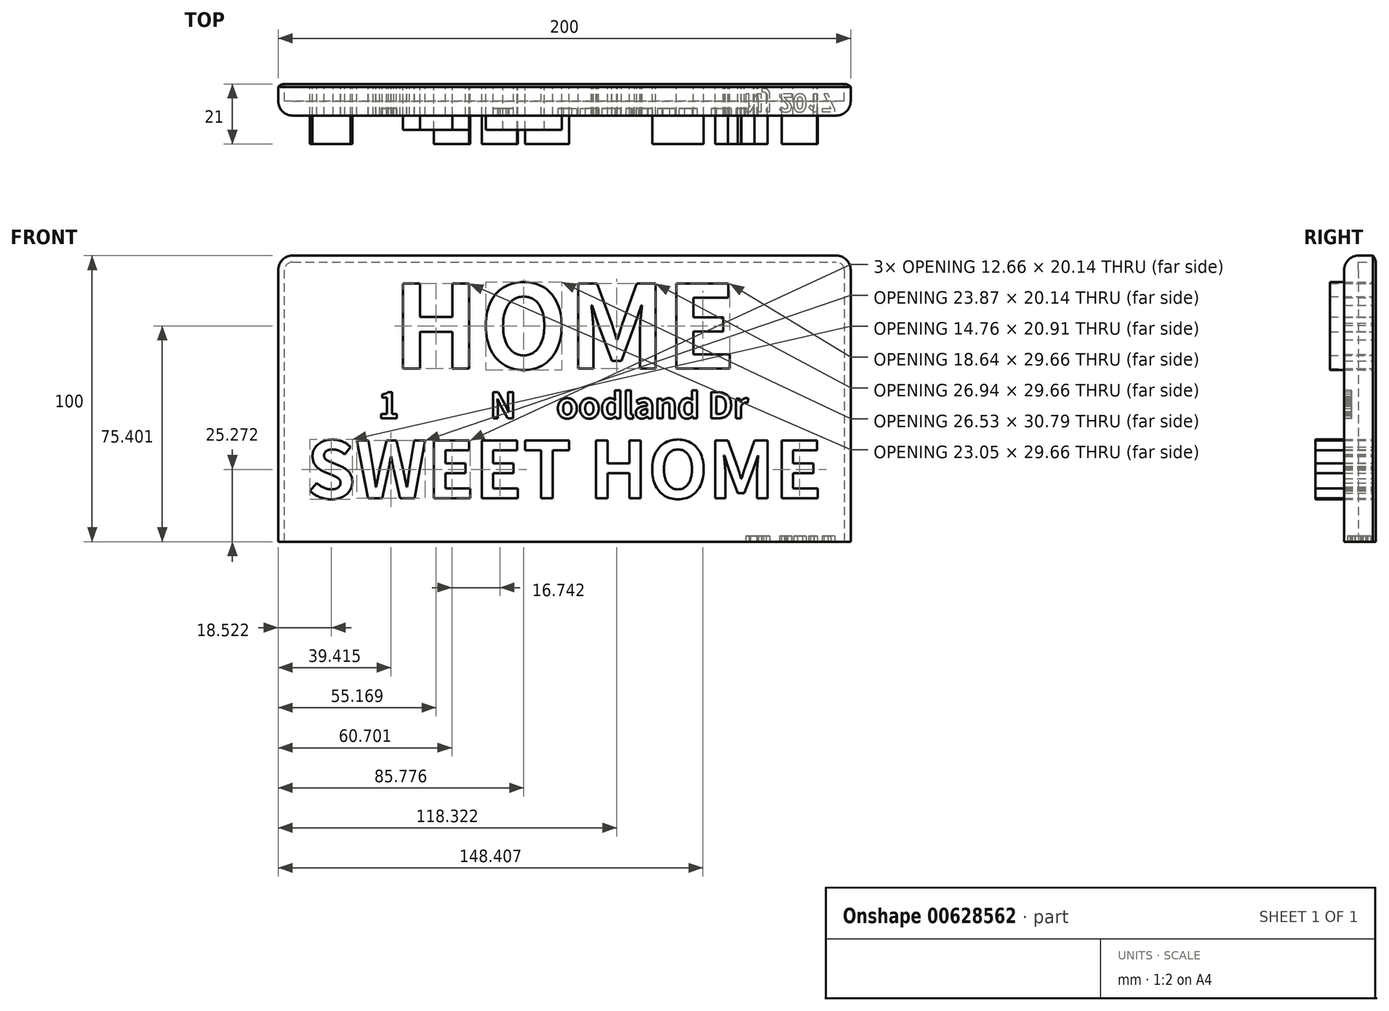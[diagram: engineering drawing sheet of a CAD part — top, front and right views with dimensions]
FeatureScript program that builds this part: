
annotation { "Feature Type Name" : "Feature", "Feature Type Description" : "" }
export const myFeature = defineFeature(function(context is Context, id is Id, definition is map)
    precondition{}
    {
        {
            var Q0;
            Q0=qCreatedBy(makeId("Front.planeOp"),FACE);
            var sketch = newSketch(context, id + "F0", { "sketchPlane" : qUnion([Q0])});
            skLineSegment(sketch, "E0.bottom", {"start": v(100, -50) * mm, "end": v(-100, -50) * mm});
            skLineSegment(sketch, "E0.top", {"start": v(100, 50) * mm, "end": v(-100, 50) * mm});
            skLineSegment(sketch, "E0.left", {"start": v(100, -50) * mm, "end": v(100, 50) * mm});
            skLineSegment(sketch, "E0.right", {"start": v(-100, -50) * mm, "end": v(-100, 50) * mm});
            skPoint(sketch, "E0.middle", {"position": v(0, 0) * mm});
            skLineSegment(sketch, "E1", {"start": v(-100, 0) * mm, "end": v(100, 0) * mm, "construction": true});
            skLineSegment(sketch, "E2", {"start": v(0, 50) * mm, "end": v(0, -50) * mm, "construction": true});
            skText(sketch, "E3", { "text": "HOME", "fontName": "NotoSansCJKsc-Bold.otf"});
            skText(sketch, "E4", { "text": "SWEET HOME", "fontName": "NotoSansCJKsc-Bold.otf"});
            skLineSegment(sketch, "E5", {"start": v(100, 50) * mm, "end": v(100, 25) * mm, "construction": true});
            skLineSegment(sketch, "E6", {"start": v(100, 25) * mm, "end": v(-100, 25) * mm, "construction": true});
            skLineSegment(sketch, "E7", {"start": v(100, 0) * mm, "end": v(100, -25) * mm, "construction": true});
            skLineSegment(sketch, "E8", {"start": v(100, -25) * mm, "end": v(-100, -25) * mm, "construction": true});
            skPoint(sketch, "E8.endSnap0", {"position": v(-90, -25) * mm});
            const initialGuessF0  = {"E3": [-0.06, 0.01057, 1, 0, 0.02886], "E4": [-0.09, -0.0348, 1, 0, 0.0196]};
            skSetInitialGuess(sketch, initialGuessF0);
            skSolve(sketch);
        }
        {
            var Q0;
            Q0=makeQuery(id+"F0.imprint","IMPRINT",FACE,{"disambiguationData":[TD([[makeQuery(id+"F0.imprint","IMPRINT",EDGE,{"derivedFrom":sQuery(id+"F0.wireOp",EDGE,"E4.sketch_text.stroke-0")}),1.0]])]});
            var Q1;
            Q1=makeQuery(id+"F0.imprint","IMPRINT",FACE,{"disambiguationData":[TD([[makeQuery(id+"F0.imprint","IMPRINT",EDGE,{"derivedFrom":sQuery(id+"F0.wireOp",EDGE,"E4.sketch_text.stroke-10")}),1.0]])]});
            var Q2;
            Q2=makeQuery(id+"F0.imprint","IMPRINT",FACE,{"disambiguationData":[TD([[makeQuery(id+"F0.imprint","IMPRINT",EDGE,{"derivedFrom":sQuery(id+"F0.wireOp",EDGE,"E4.sketch_text.stroke-22")}),1.0]])]});
            var Q3;
            Q3=makeQuery(id+"F0.imprint","IMPRINT",FACE,{"disambiguationData":[TD([[makeQuery(id+"F0.imprint","IMPRINT",EDGE,{"derivedFrom":sQuery(id+"F0.wireOp",EDGE,"E4.sketch_text.stroke-32")}),1.0]])]});
            var Q4;
            Q4=makeQuery(id+"F0.imprint","IMPRINT",FACE,{"disambiguationData":[TD([[makeQuery(id+"F0.imprint","IMPRINT",EDGE,{"derivedFrom":sQuery(id+"F0.wireOp",EDGE,"E4.sketch_text.stroke-38")}),1.0]])]});
            var Q5;
            Q5=makeQuery(id+"F0.imprint","IMPRINT",FACE,{"disambiguationData":[TD([[makeQuery(id+"F0.imprint","IMPRINT",EDGE,{"derivedFrom":sQuery(id+"F0.wireOp",EDGE,"E4.sketch_text.stroke-46")}),1.0]])]});
            var Q6;
            Q6=makeQuery(id+"F0.imprint","IMPRINT",FACE,{"disambiguationData":[TD([[makeQuery(id+"F0.imprint","IMPRINT",EDGE,{"derivedFrom":sQuery(id+"F0.wireOp",EDGE,"E4.sketch_text.stroke-62")}),1.0]])]});
            var Q7;
            Q7=makeQuery(id+"F0.imprint","IMPRINT",FACE,{"disambiguationData":[TD([[makeQuery(id+"F0.imprint","IMPRINT",EDGE,{"derivedFrom":sQuery(id+"F0.wireOp",EDGE,"E4.sketch_text.stroke-74")}),1.0]])]});
            var Q8;
            Q8=makeQuery(id+"F0.imprint","IMPRINT",FACE,{"disambiguationData":[TD([[makeQuery(id+"F0.imprint","IMPRINT",EDGE,{"derivedFrom":sQuery(id+"F0.wireOp",EDGE,"E4.sketch_text.stroke-50")}),1.0]])]});
            var Q9;
            Q9=makeQuery(id+"F0.imprint","IMPRINT",FACE,{"disambiguationData":[TD([[makeQuery(id+"F0.imprint","IMPRINT",EDGE,{"derivedFrom":sQuery(id+"F0.wireOp",EDGE,"E4.sketch_text.stroke-82")}),1.0]])]});
            var Q10;
            Q10=makeQuery(id+"F0.imprint","IMPRINT",FACE,{"disambiguationData":[TD([[makeQuery(id+"F0.imprint","IMPRINT",EDGE,{"derivedFrom":sQuery(id+"F0.wireOp",EDGE,"E4.sketch_text.stroke-90")}),1.0]])]});
            var Q11;
            Q11=makeQuery(id+"F0.imprint","IMPRINT",FACE,{"disambiguationData":[TD([[makeQuery(id+"F0.imprint","IMPRINT",EDGE,{"derivedFrom":sQuery(id+"F0.wireOp",EDGE,"E4.sketch_text.stroke-112")}),1.0]])]});
            extrude(context, id + "F1", {"entities" : qUnion([Q0, Q1, Q2, Q3, Q4, Q5, Q6, Q7, Q8, Q9, Q10, Q11]), "depth" : 20 * mm, "offsetDistance" : 25 * mm});
        }
        {
            var Q0;
            Q0=makeQuery(id+"F0.imprint","IMPRINT",FACE,{"disambiguationData":[TD([[makeQuery(id+"F0.imprint","IMPRINT",EDGE,{"derivedFrom":sQuery(id+"F0.wireOp",EDGE,"E3.sketch_text.stroke-0")}),1.0]])]});
            var Q1;
            Q1=makeQuery(id+"F0.imprint","IMPRINT",FACE,{"disambiguationData":[TD([[makeQuery(id+"F0.imprint","IMPRINT",EDGE,{"derivedFrom":sQuery(id+"F0.wireOp",EDGE,"E3.sketch_text.stroke-4")}),1.0]])]});
            var Q2;
            Q2=makeQuery(id+"F0.imprint","IMPRINT",FACE,{"disambiguationData":[TD([[makeQuery(id+"F0.imprint","IMPRINT",EDGE,{"derivedFrom":sQuery(id+"F0.wireOp",EDGE,"E3.sketch_text.stroke-12")}),1.0]])]});
            var Q3;
            Q3=makeQuery(id+"F0.imprint","IMPRINT",FACE,{"disambiguationData":[TD([[makeQuery(id+"F0.imprint","IMPRINT",EDGE,{"derivedFrom":sQuery(id+"F0.wireOp",EDGE,"E3.sketch_text.stroke-34")}),1.0]])]});
            var Q4;
            Q4=makeQuery(id+"F0.imprint","IMPRINT",FACE,{"disambiguationData":[TD([[makeQuery(id+"F0.imprint","IMPRINT",EDGE,{"derivedFrom":sQuery(id+"F0.wireOp",EDGE,"E3.sketch_text.stroke-48")}),1.0]])]});
            var Q5;
            Q5=makeQuery(id+"F0.imprint","IMPRINT",FACE,{"disambiguationData":[TD([[makeQuery(id+"F0.imprint","IMPRINT",EDGE,{"derivedFrom":sQuery(id+"F0.wireOp",EDGE,"E3.sketch_text.stroke-64")}),1.0]])]});
            var Q6;
            Q6=makeQuery(id+"F0.imprint","IMPRINT",FACE,{"disambiguationData":[TD([[makeQuery(id+"F0.imprint","IMPRINT",EDGE,{"derivedFrom":sQuery(id+"F0.wireOp",EDGE,"E3.sketch_text.stroke-72")}),1.0]])]});
            var Q7;
            Q7=makeQuery(id+"F0.imprint","IMPRINT",FACE,{"disambiguationData":[TD([[makeQuery(id+"F0.imprint","IMPRINT",EDGE,{"derivedFrom":sQuery(id+"F0.wireOp",EDGE,"E3.sketch_text.stroke-86")}),1.0]])]});
            var Q8;
            Q8=makeQuery(id+"F0.imprint","IMPRINT",FACE,{"disambiguationData":[TD([[makeQuery(id+"F0.imprint","IMPRINT",EDGE,{"derivedFrom":sQuery(id+"F0.wireOp",EDGE,"E3.sketch_text.stroke-94")}),1.0]])]});
            extrude(context, id + "F2", {"entities" : qUnion([Q0, Q1, Q2, Q3, Q4, Q5, Q6, Q7, Q8]), "depth" : 15 * mm, "offsetDistance" : 25 * mm});
        }
        {
            var Q0;
            Q0=makeQuery(id+"F0.imprint","IMPRINT",FACE,{"disambiguationData":[TD([[makeQuery(id+"F0.imprint","IMPRINT",EDGE,{"derivedFrom":sQuery(id+"F0.wireOp",EDGE,"E3.sketch_text.stroke-8")}),-1.0]])]});
            var Q1;
            Q1=makeQuery(id+"F0.imprint","IMPRINT",FACE,{"disambiguationData":[TD([[makeQuery(id+"F0.imprint","IMPRINT",EDGE,{"derivedFrom":sQuery(id+"F0.wireOp",EDGE,"E3.sketch_text.stroke-34")}),-1.0]])]});
            var Q2;
            Q2=makeQuery(id+"F0.imprint","IMPRINT",FACE,{"disambiguationData":[TD([[makeQuery(id+"F0.imprint","IMPRINT",EDGE,{"derivedFrom":sQuery(id+"F0.wireOp",EDGE,"E3.sketch_text.stroke-72")}),-1.0]])]});
            var Q3;
            Q3=makeQuery(id+"F0.imprint","IMPRINT",FACE,{"disambiguationData":[TD([[makeQuery(id+"F0.imprint","IMPRINT",EDGE,{"derivedFrom":sQuery(id+"F0.wireOp",EDGE,"E4.sketch_text.stroke-42")}),-1.0]])]});
            var Q4;
            Q4=makeQuery(id+"F0.imprint","IMPRINT",FACE,{"disambiguationData":[TD([[makeQuery(id+"F0.imprint","IMPRINT",EDGE,{"derivedFrom":sQuery(id+"F0.wireOp",EDGE,"E0.bottom")}),-1.0]])]});
            extrude(context, id + "F3", {"entities" : qUnion([Q0, Q1, Q2, Q3, Q4]), "depth" : 10 * mm, "offsetDistance" : 25 * mm});
        }
        {
            var Q0;
            Q0=makeQuery(id+"F3.opExtrude","CAP_FACE",FACE,{"disambiguationData":[OSD([sQuery(id+"F0.wireOp",EDGE,"E0.bottom"),sQuery(id+"F0.wireOp",EDGE,"E0.top"),sQuery(id+"F0.wireOp",EDGE,"E0.left"),sQuery(id+"F0.wireOp",EDGE,"E0.right"),sQuery(id+"F0.wireOp",EDGE,"E3.sketch_text.stroke-0"),sQuery(id+"F0.wireOp",EDGE,"E3.sketch_text.stroke-1"),sQuery(id+"F0.wireOp",EDGE,"E3.sketch_text.stroke-2"),sQuery(id+"F0.wireOp",EDGE,"E3.sketch_text.stroke-3"),sQuery(id+"F0.wireOp",EDGE,"E3.sketch_text.stroke-4"),sQuery(id+"F0.wireOp",EDGE,"E3.sketch_text.stroke-5"),sQuery(id+"F0.wireOp",EDGE,"E3.sketch_text.stroke-6"),sQuery(id+"F0.wireOp",EDGE,"E3.sketch_text.stroke-7"),sQuery(id+"F0.wireOp",EDGE,"E3.sketch_text.stroke-12"),sQuery(id+"F0.wireOp",EDGE,"E3.sketch_text.stroke-13"),sQuery(id+"F0.wireOp",EDGE,"E3.sketch_text.stroke-14"),sQuery(id+"F0.wireOp",EDGE,"E3.sketch_text.stroke-15"),sQuery(id+"F0.wireOp",EDGE,"E3.sketch_text.stroke-16"),sQuery(id+"F0.wireOp",EDGE,"E3.sketch_text.stroke-17"),sQuery(id+"F0.wireOp",EDGE,"E3.sketch_text.stroke-18"),sQuery(id+"F0.wireOp",EDGE,"E3.sketch_text.stroke-19"),sQuery(id+"F0.wireOp",EDGE,"E3.sketch_text.stroke-20"),sQuery(id+"F0.wireOp",EDGE,"E3.sketch_text.stroke-21"),sQuery(id+"F0.wireOp",EDGE,"E3.sketch_text.stroke-22"),sQuery(id+"F0.wireOp",EDGE,"E3.sketch_text.stroke-23"),sQuery(id+"F0.wireOp",EDGE,"E3.sketch_text.stroke-24"),sQuery(id+"F0.wireOp",EDGE,"E3.sketch_text.stroke-25"),sQuery(id+"F0.wireOp",EDGE,"E3.sketch_text.stroke-26"),sQuery(id+"F0.wireOp",EDGE,"E3.sketch_text.stroke-27"),sQuery(id+"F0.wireOp",EDGE,"E3.sketch_text.stroke-28"),sQuery(id+"F0.wireOp",EDGE,"E3.sketch_text.stroke-29"),sQuery(id+"F0.wireOp",EDGE,"E3.sketch_text.stroke-30"),sQuery(id+"F0.wireOp",EDGE,"E3.sketch_text.stroke-31"),sQuery(id+"F0.wireOp",EDGE,"E3.sketch_text.stroke-32"),sQuery(id+"F0.wireOp",EDGE,"E3.sketch_text.stroke-33"),sQuery(id+"F0.wireOp",EDGE,"E3.sketch_text.stroke-40"),sQuery(id+"F0.wireOp",EDGE,"E3.sketch_text.stroke-41"),sQuery(id+"F0.wireOp",EDGE,"E3.sketch_text.stroke-42"),sQuery(id+"F0.wireOp",EDGE,"E3.sketch_text.stroke-43"),sQuery(id+"F0.wireOp",EDGE,"E3.sketch_text.stroke-44"),sQuery(id+"F0.wireOp",EDGE,"E3.sketch_text.stroke-45"),sQuery(id+"F0.wireOp",EDGE,"E3.sketch_text.stroke-46"),sQuery(id+"F0.wireOp",EDGE,"E3.sketch_text.stroke-47"),sQuery(id+"F0.wireOp",EDGE,"E3.sketch_text.stroke-48"),sQuery(id+"F0.wireOp",EDGE,"E3.sketch_text.stroke-49"),sQuery(id+"F0.wireOp",EDGE,"E3.sketch_text.stroke-50"),sQuery(id+"F0.wireOp",EDGE,"E3.sketch_text.stroke-51"),sQuery(id+"F0.wireOp",EDGE,"E3.sketch_text.stroke-52"),sQuery(id+"F0.wireOp",EDGE,"E3.sketch_text.stroke-53"),sQuery(id+"F0.wireOp",EDGE,"E3.sketch_text.stroke-54"),sQuery(id+"F0.wireOp",EDGE,"E3.sketch_text.stroke-55"),sQuery(id+"F0.wireOp",EDGE,"E3.sketch_text.stroke-56"),sQuery(id+"F0.wireOp",EDGE,"E3.sketch_text.stroke-57"),sQuery(id+"F0.wireOp",EDGE,"E3.sketch_text.stroke-58"),sQuery(id+"F0.wireOp",EDGE,"E3.sketch_text.stroke-59"),sQuery(id+"F0.wireOp",EDGE,"E3.sketch_text.stroke-60"),sQuery(id+"F0.wireOp",EDGE,"E3.sketch_text.stroke-61"),sQuery(id+"F0.wireOp",EDGE,"E3.sketch_text.stroke-62"),sQuery(id+"F0.wireOp",EDGE,"E3.sketch_text.stroke-63"),sQuery(id+"F0.wireOp",EDGE,"E3.sketch_text.stroke-64"),sQuery(id+"F0.wireOp",EDGE,"E3.sketch_text.stroke-65"),sQuery(id+"F0.wireOp",EDGE,"E3.sketch_text.stroke-66"),sQuery(id+"F0.wireOp",EDGE,"E3.sketch_text.stroke-67"),sQuery(id+"F0.wireOp",EDGE,"E3.sketch_text.stroke-68"),sQuery(id+"F0.wireOp",EDGE,"E3.sketch_text.stroke-69"),sQuery(id+"F0.wireOp",EDGE,"E3.sketch_text.stroke-70"),sQuery(id+"F0.wireOp",EDGE,"E3.sketch_text.stroke-71"),sQuery(id+"F0.wireOp",EDGE,"E3.sketch_text.stroke-78"),sQuery(id+"F0.wireOp",EDGE,"E3.sketch_text.stroke-79"),sQuery(id+"F0.wireOp",EDGE,"E3.sketch_text.stroke-80"),sQuery(id+"F0.wireOp",EDGE,"E3.sketch_text.stroke-81"),sQuery(id+"F0.wireOp",EDGE,"E3.sketch_text.stroke-82"),sQuery(id+"F0.wireOp",EDGE,"E3.sketch_text.stroke-83"),sQuery(id+"F0.wireOp",EDGE,"E3.sketch_text.stroke-84"),sQuery(id+"F0.wireOp",EDGE,"E3.sketch_text.stroke-85"),sQuery(id+"F0.wireOp",EDGE,"E3.sketch_text.stroke-86"),sQuery(id+"F0.wireOp",EDGE,"E3.sketch_text.stroke-87"),sQuery(id+"F0.wireOp",EDGE,"E3.sketch_text.stroke-88"),sQuery(id+"F0.wireOp",EDGE,"E3.sketch_text.stroke-89"),sQuery(id+"F0.wireOp",EDGE,"E3.sketch_text.stroke-90"),sQuery(id+"F0.wireOp",EDGE,"E3.sketch_text.stroke-91"),sQuery(id+"F0.wireOp",EDGE,"E3.sketch_text.stroke-92"),sQuery(id+"F0.wireOp",EDGE,"E3.sketch_text.stroke-93"),sQuery(id+"F0.wireOp",EDGE,"E3.sketch_text.stroke-94"),sQuery(id+"F0.wireOp",EDGE,"E3.sketch_text.stroke-95"),sQuery(id+"F0.wireOp",EDGE,"E3.sketch_text.stroke-96"),sQuery(id+"F0.wireOp",EDGE,"E3.sketch_text.stroke-97"),sQuery(id+"F0.wireOp",EDGE,"E3.sketch_text.stroke-98"),sQuery(id+"F0.wireOp",EDGE,"E3.sketch_text.stroke-99"),sQuery(id+"F0.wireOp",EDGE,"E3.sketch_text.stroke-100"),sQuery(id+"F0.wireOp",EDGE,"E3.sketch_text.stroke-101"),sQuery(id+"F0.wireOp",EDGE,"E3.sketch_text.stroke-102"),sQuery(id+"F0.wireOp",EDGE,"E3.sketch_text.stroke-103"),sQuery(id+"F0.wireOp",EDGE,"E3.sketch_text.stroke-104"),sQuery(id+"F0.wireOp",EDGE,"E3.sketch_text.stroke-105"),sQuery(id+"F0.wireOp",EDGE,"E4.sketch_text.stroke-0"),sQuery(id+"F0.wireOp",EDGE,"E4.sketch_text.stroke-1"),sQuery(id+"F0.wireOp",EDGE,"E4.sketch_text.stroke-2"),sQuery(id+"F0.wireOp",EDGE,"E4.sketch_text.stroke-3"),sQuery(id+"F0.wireOp",EDGE,"E4.sketch_text.stroke-4"),sQuery(id+"F0.wireOp",EDGE,"E4.sketch_text.stroke-5"),sQuery(id+"F0.wireOp",EDGE,"E4.sketch_text.stroke-6"),sQuery(id+"F0.wireOp",EDGE,"E4.sketch_text.stroke-7"),sQuery(id+"F0.wireOp",EDGE,"E4.sketch_text.stroke-8"),sQuery(id+"F0.wireOp",EDGE,"E4.sketch_text.stroke-9"),sQuery(id+"F0.wireOp",EDGE,"E4.sketch_text.stroke-10"),sQuery(id+"F0.wireOp",EDGE,"E4.sketch_text.stroke-11"),sQuery(id+"F0.wireOp",EDGE,"E4.sketch_text.stroke-12"),sQuery(id+"F0.wireOp",EDGE,"E4.sketch_text.stroke-13"),sQuery(id+"F0.wireOp",EDGE,"E4.sketch_text.stroke-14"),sQuery(id+"F0.wireOp",EDGE,"E4.sketch_text.stroke-15"),sQuery(id+"F0.wireOp",EDGE,"E4.sketch_text.stroke-16"),sQuery(id+"F0.wireOp",EDGE,"E4.sketch_text.stroke-17"),sQuery(id+"F0.wireOp",EDGE,"E4.sketch_text.stroke-18"),sQuery(id+"F0.wireOp",EDGE,"E4.sketch_text.stroke-19"),sQuery(id+"F0.wireOp",EDGE,"E4.sketch_text.stroke-20"),sQuery(id+"F0.wireOp",EDGE,"E4.sketch_text.stroke-21"),sQuery(id+"F0.wireOp",EDGE,"E4.sketch_text.stroke-22"),sQuery(id+"F0.wireOp",EDGE,"E4.sketch_text.stroke-23"),sQuery(id+"F0.wireOp",EDGE,"E4.sketch_text.stroke-24"),sQuery(id+"F0.wireOp",EDGE,"E4.sketch_text.stroke-25"),sQuery(id+"F0.wireOp",EDGE,"E4.sketch_text.stroke-26"),sQuery(id+"F0.wireOp",EDGE,"E4.sketch_text.stroke-27"),sQuery(id+"F0.wireOp",EDGE,"E4.sketch_text.stroke-28"),sQuery(id+"F0.wireOp",EDGE,"E4.sketch_text.stroke-29"),sQuery(id+"F0.wireOp",EDGE,"E4.sketch_text.stroke-30"),sQuery(id+"F0.wireOp",EDGE,"E4.sketch_text.stroke-31"),sQuery(id+"F0.wireOp",EDGE,"E4.sketch_text.stroke-32"),sQuery(id+"F0.wireOp",EDGE,"E4.sketch_text.stroke-33"),sQuery(id+"F0.wireOp",EDGE,"E4.sketch_text.stroke-34"),sQuery(id+"F0.wireOp",EDGE,"E4.sketch_text.stroke-35"),sQuery(id+"F0.wireOp",EDGE,"E4.sketch_text.stroke-36"),sQuery(id+"F0.wireOp",EDGE,"E4.sketch_text.stroke-37"),sQuery(id+"F0.wireOp",EDGE,"E4.sketch_text.stroke-38"),sQuery(id+"F0.wireOp",EDGE,"E4.sketch_text.stroke-39"),sQuery(id+"F0.wireOp",EDGE,"E4.sketch_text.stroke-40"),sQuery(id+"F0.wireOp",EDGE,"E4.sketch_text.stroke-41"),sQuery(id+"F0.wireOp",EDGE,"E4.sketch_text.stroke-46"),sQuery(id+"F0.wireOp",EDGE,"E4.sketch_text.stroke-47"),sQuery(id+"F0.wireOp",EDGE,"E4.sketch_text.stroke-48"),sQuery(id+"F0.wireOp",EDGE,"E4.sketch_text.stroke-49"),sQuery(id+"F0.wireOp",EDGE,"E4.sketch_text.stroke-50"),sQuery(id+"F0.wireOp",EDGE,"E4.sketch_text.stroke-51"),sQuery(id+"F0.wireOp",EDGE,"E4.sketch_text.stroke-52"),sQuery(id+"F0.wireOp",EDGE,"E4.sketch_text.stroke-53"),sQuery(id+"F0.wireOp",EDGE,"E4.sketch_text.stroke-54"),sQuery(id+"F0.wireOp",EDGE,"E4.sketch_text.stroke-55"),sQuery(id+"F0.wireOp",EDGE,"E4.sketch_text.stroke-56"),sQuery(id+"F0.wireOp",EDGE,"E4.sketch_text.stroke-57"),sQuery(id+"F0.wireOp",EDGE,"E4.sketch_text.stroke-58"),sQuery(id+"F0.wireOp",EDGE,"E4.sketch_text.stroke-59"),sQuery(id+"F0.wireOp",EDGE,"E4.sketch_text.stroke-60"),sQuery(id+"F0.wireOp",EDGE,"E4.sketch_text.stroke-61"),sQuery(id+"F0.wireOp",EDGE,"E4.sketch_text.stroke-62"),sQuery(id+"F0.wireOp",EDGE,"E4.sketch_text.stroke-63"),sQuery(id+"F0.wireOp",EDGE,"E4.sketch_text.stroke-64"),sQuery(id+"F0.wireOp",EDGE,"E4.sketch_text.stroke-65"),sQuery(id+"F0.wireOp",EDGE,"E4.sketch_text.stroke-66"),sQuery(id+"F0.wireOp",EDGE,"E4.sketch_text.stroke-67"),sQuery(id+"F0.wireOp",EDGE,"E4.sketch_text.stroke-68"),sQuery(id+"F0.wireOp",EDGE,"E4.sketch_text.stroke-69"),sQuery(id+"F0.wireOp",EDGE,"E4.sketch_text.stroke-70"),sQuery(id+"F0.wireOp",EDGE,"E4.sketch_text.stroke-71"),sQuery(id+"F0.wireOp",EDGE,"E4.sketch_text.stroke-72"),sQuery(id+"F0.wireOp",EDGE,"E4.sketch_text.stroke-73"),sQuery(id+"F0.wireOp",EDGE,"E4.sketch_text.stroke-74"),sQuery(id+"F0.wireOp",EDGE,"E4.sketch_text.stroke-75"),sQuery(id+"F0.wireOp",EDGE,"E4.sketch_text.stroke-76"),sQuery(id+"F0.wireOp",EDGE,"E4.sketch_text.stroke-77"),sQuery(id+"F0.wireOp",EDGE,"E4.sketch_text.stroke-78"),sQuery(id+"F0.wireOp",EDGE,"E4.sketch_text.stroke-79"),sQuery(id+"F0.wireOp",EDGE,"E4.sketch_text.stroke-80"),sQuery(id+"F0.wireOp",EDGE,"E4.sketch_text.stroke-81"),sQuery(id+"F0.wireOp",EDGE,"E4.sketch_text.stroke-82"),sQuery(id+"F0.wireOp",EDGE,"E4.sketch_text.stroke-83"),sQuery(id+"F0.wireOp",EDGE,"E4.sketch_text.stroke-84"),sQuery(id+"F0.wireOp",EDGE,"E4.sketch_text.stroke-85"),sQuery(id+"F0.wireOp",EDGE,"E4.sketch_text.stroke-86"),sQuery(id+"F0.wireOp",EDGE,"E4.sketch_text.stroke-87"),sQuery(id+"F0.wireOp",EDGE,"E4.sketch_text.stroke-88"),sQuery(id+"F0.wireOp",EDGE,"E4.sketch_text.stroke-89")])],"isStart":false});
            var sketch = newSketch(context, id + "F4", { "sketchPlane" : qUnion([Q0])});
            skText(sketch, "E9", { "text": "12524 N Woodland Dr", "fontName": "NotoSansCJKkr-Bold.otf"});
            skLineSegment(sketch, "E10", {"start": v(-100, 50) * mm, "end": v(100, 50) * mm, "construction": true});
            skLineSegment(sketch, "E11", {"start": v(100, 50) * mm, "end": v(100, -50) * mm, "construction": true});
            skLineSegment(sketch, "E12", {"start": v(100, -50) * mm, "end": v(-100, -50) * mm, "construction": true});
            skLineSegment(sketch, "E13", {"start": v(-100, -50) * mm, "end": v(-100, 50) * mm, "construction": true});
            skLineSegment(sketch, "E14", {"start": v(0, 50) * mm, "end": v(0, -50) * mm, "construction": true});
            skLineSegment(sketch, "E15", {"start": v(-100, 0) * mm, "end": v(100, 0) * mm, "construction": true});
            const initialGuessF4  = {"E9": [-0.065, -0.00684, 1, 0, 0.00884]};
            skSetInitialGuess(sketch, initialGuessF4);
            skSolve(sketch);
        }
        {
            var Q0;
            Q0=makeQuery(id+"F4.imprint","IMPRINT",FACE,{"disambiguationData":[TD([[makeQuery(id+"F4.imprint","IMPRINT",EDGE,{"derivedFrom":sQuery(id+"F4.wireOp",EDGE,"E9.sketch_text.stroke-0")}),1.0]])]});
            var Q1;
            Q1=makeQuery(id+"F4.imprint","IMPRINT",FACE,{"disambiguationData":[TD([[makeQuery(id+"F4.imprint","IMPRINT",EDGE,{"derivedFrom":sQuery(id+"F4.wireOp",EDGE,"E9.sketch_text.stroke-14")}),1.0]])]});
            var Q2;
            Q2=makeQuery(id+"F4.imprint","IMPRINT",FACE,{"disambiguationData":[TD([[makeQuery(id+"F4.imprint","IMPRINT",EDGE,{"derivedFrom":sQuery(id+"F4.wireOp",EDGE,"E9.sketch_text.stroke-29")}),1.0]])]});
            var Q3;
            Q3=makeQuery(id+"F4.imprint","IMPRINT",FACE,{"disambiguationData":[TD([[makeQuery(id+"F4.imprint","IMPRINT",EDGE,{"derivedFrom":sQuery(id+"F4.wireOp",EDGE,"E9.sketch_text.stroke-43")}),1.0]])]});
            var Q4;
            Q4=makeQuery(id+"F4.imprint","IMPRINT",FACE,{"disambiguationData":[TD([[makeQuery(id+"F4.imprint","IMPRINT",EDGE,{"derivedFrom":sQuery(id+"F4.wireOp",EDGE,"E9.sketch_text.stroke-59")}),1.0]])]});
            var Q5;
            Q5=makeQuery(id+"F4.imprint","IMPRINT",FACE,{"disambiguationData":[TD([[makeQuery(id+"F4.imprint","IMPRINT",EDGE,{"derivedFrom":sQuery(id+"F4.wireOp",EDGE,"E9.sketch_text.stroke-69")}),1.0]])]});
            var Q6;
            Q6=makeQuery(id+"F4.imprint","IMPRINT",FACE,{"disambiguationData":[TD([[makeQuery(id+"F4.imprint","IMPRINT",EDGE,{"derivedFrom":sQuery(id+"F4.wireOp",EDGE,"E9.sketch_text.stroke-91")}),1.0]])]});
            var Q7;
            Q7=makeQuery(id+"F4.imprint","IMPRINT",FACE,{"disambiguationData":[TD([[makeQuery(id+"F4.imprint","IMPRINT",EDGE,{"derivedFrom":sQuery(id+"F4.wireOp",EDGE,"E9.sketch_text.stroke-105")}),1.0]])]});
            var Q8;
            Q8=makeQuery(id+"F4.imprint","IMPRINT",FACE,{"disambiguationData":[TD([[makeQuery(id+"F4.imprint","IMPRINT",EDGE,{"derivedFrom":sQuery(id+"F4.wireOp",EDGE,"E9.sketch_text.stroke-113")}),1.0]])]});
            var Q9;
            Q9=makeQuery(id+"F4.imprint","IMPRINT",FACE,{"disambiguationData":[TD([[makeQuery(id+"F4.imprint","IMPRINT",EDGE,{"derivedFrom":sQuery(id+"F4.wireOp",EDGE,"E9.sketch_text.stroke-121")}),1.0]])]});
            var Q10;
            Q10=makeQuery(id+"F4.imprint","IMPRINT",FACE,{"disambiguationData":[TD([[makeQuery(id+"F4.imprint","IMPRINT",EDGE,{"derivedFrom":sQuery(id+"F4.wireOp",EDGE,"E9.sketch_text.stroke-137")}),1.0]])]});
            var Q11;
            Q11=makeQuery(id+"F4.imprint","IMPRINT",FACE,{"disambiguationData":[TD([[makeQuery(id+"F4.imprint","IMPRINT",EDGE,{"derivedFrom":sQuery(id+"F4.wireOp",EDGE,"E9.sketch_text.stroke-145")}),1.0]])]});
            var Q12;
            Q12=makeQuery(id+"F4.imprint","IMPRINT",FACE,{"disambiguationData":[TD([[makeQuery(id+"F4.imprint","IMPRINT",EDGE,{"derivedFrom":sQuery(id+"F4.wireOp",EDGE,"E9.sketch_text.stroke-161")}),1.0]])]});
            var Q13;
            Q13=makeQuery(id+"F4.imprint","IMPRINT",FACE,{"disambiguationData":[TD([[makeQuery(id+"F4.imprint","IMPRINT",EDGE,{"derivedFrom":sQuery(id+"F4.wireOp",EDGE,"E9.sketch_text.stroke-174")}),1.0]])]});
            var Q14;
            Q14=makeQuery(id+"F4.imprint","IMPRINT",FACE,{"disambiguationData":[TD([[makeQuery(id+"F4.imprint","IMPRINT",EDGE,{"derivedFrom":sQuery(id+"F4.wireOp",EDGE,"E9.sketch_text.stroke-190")}),1.0]])]});
            var Q15;
            Q15=makeQuery(id+"F4.imprint","IMPRINT",FACE,{"disambiguationData":[TD([[makeQuery(id+"F4.imprint","IMPRINT",EDGE,{"derivedFrom":sQuery(id+"F4.wireOp",EDGE,"E9.sketch_text.stroke-200")}),1.0]])]});
            extrude(context, id + "F5", {"entities" : qUnion([Q0, Q1, Q2, Q3, Q4, Q5, Q6, Q7, Q8, Q9, Q10, Q11, Q12, Q13, Q14, Q15]), "operationType" : NewBodyOperationType.REMOVE, "depth" : -5 * mm, "offsetDistance" : 25 * mm, "symmetric" : true});
        }
        {
            var Q0;
            Q0=makeQuery(id+"F3.opExtrude","CAP_EDGE",EDGE,{"disambiguationData":[OSD([sQuery(id+"F0.wireOp",EDGE,"E0.right")])],"isStart":false});
            var Q1;
            Q1=makeQuery(id+"F3.opExtrude","CAP_EDGE",EDGE,{"disambiguationData":[OSD([sQuery(id+"F0.wireOp",EDGE,"E0.top")])],"isStart":false});
            fillet(context, id + "F6", {"entities" : qUnion([Q0, Q1]), "radius" : 5 * mm, "tangentPropagation" : true, "allowEdgeOverflow" : false});
        }
        {
            var Q0;
            {var subQ0=sQuery(id+"F0.wireOp",EDGE,"E3.sketch_text.stroke-54");var subQ1=sQuery(id+"F0.wireOp",EDGE,"E4.sketch_text.stroke-81");var subQ2=sQuery(id+"F0.wireOp",EDGE,"E4.sketch_text.stroke-80");var subQ3=sQuery(id+"F0.wireOp",EDGE,"E4.sketch_text.stroke-78");var subQ4=sQuery(id+"F0.wireOp",EDGE,"E4.sketch_text.stroke-77");var subQ5=sQuery(id+"F0.wireOp",EDGE,"E4.sketch_text.stroke-76");var subQ6=sQuery(id+"F0.wireOp",EDGE,"E4.sketch_text.stroke-75");var subQ7=sQuery(id+"F0.wireOp",EDGE,"E4.sketch_text.stroke-74");var subQ8=sQuery(id+"F0.wireOp",EDGE,"E4.sketch_text.stroke-73");var subQ9=sQuery(id+"F0.wireOp",EDGE,"E4.sketch_text.stroke-72");var subQ10=sQuery(id+"F0.wireOp",EDGE,"E4.sketch_text.stroke-71");var subQ11=sQuery(id+"F0.wireOp",EDGE,"E4.sketch_text.stroke-70");var subQ12=sQuery(id+"F0.wireOp",EDGE,"E4.sketch_text.stroke-69");var subQ13=sQuery(id+"F0.wireOp",EDGE,"E4.sketch_text.stroke-68");var subQ14=sQuery(id+"F0.wireOp",EDGE,"E4.sketch_text.stroke-67");var subQ15=sQuery(id+"F0.wireOp",EDGE,"E4.sketch_text.stroke-66");var subQ16=sQuery(id+"F0.wireOp",EDGE,"E4.sketch_text.stroke-65");var subQ17=sQuery(id+"F0.wireOp",EDGE,"E4.sketch_text.stroke-64");var subQ18=sQuery(id+"F0.wireOp",EDGE,"E4.sketch_text.stroke-63");var subQ19=sQuery(id+"F0.wireOp",EDGE,"E4.sketch_text.stroke-62");var subQ20=sQuery(id+"F0.wireOp",EDGE,"E4.sketch_text.stroke-61");var subQ21=sQuery(id+"F0.wireOp",EDGE,"E4.sketch_text.stroke-60");var subQ22=sQuery(id+"F0.wireOp",EDGE,"E4.sketch_text.stroke-59");var subQ23=sQuery(id+"F0.wireOp",EDGE,"E4.sketch_text.stroke-58");var subQ24=sQuery(id+"F0.wireOp",EDGE,"E4.sketch_text.stroke-57");var subQ25=sQuery(id+"F0.wireOp",EDGE,"E4.sketch_text.stroke-56");var subQ26=sQuery(id+"F0.wireOp",EDGE,"E4.sketch_text.stroke-55");var subQ27=sQuery(id+"F0.wireOp",EDGE,"E4.sketch_text.stroke-54");var subQ28=sQuery(id+"F0.wireOp",EDGE,"E4.sketch_text.stroke-53");var subQ29=sQuery(id+"F0.wireOp",EDGE,"E4.sketch_text.stroke-52");var subQ30=sQuery(id+"F0.wireOp",EDGE,"E4.sketch_text.stroke-51");var subQ31=sQuery(id+"F0.wireOp",EDGE,"E4.sketch_text.stroke-50");var subQ32=sQuery(id+"F0.wireOp",EDGE,"E4.sketch_text.stroke-49");var subQ33=sQuery(id+"F0.wireOp",EDGE,"E4.sketch_text.stroke-48");var subQ34=sQuery(id+"F0.wireOp",EDGE,"E4.sketch_text.stroke-47");var subQ35=sQuery(id+"F0.wireOp",EDGE,"E4.sketch_text.stroke-46");var subQ36=sQuery(id+"F0.wireOp",EDGE,"E4.sketch_text.stroke-41");var subQ37=sQuery(id+"F0.wireOp",EDGE,"E4.sketch_text.stroke-40");var subQ38=sQuery(id+"F0.wireOp",EDGE,"E4.sketch_text.stroke-39");var subQ39=sQuery(id+"F0.wireOp",EDGE,"E4.sketch_text.stroke-38");var subQ40=sQuery(id+"F0.wireOp",EDGE,"E4.sketch_text.stroke-37");var subQ41=sQuery(id+"F0.wireOp",EDGE,"E4.sketch_text.stroke-36");var subQ42=sQuery(id+"F0.wireOp",EDGE,"E4.sketch_text.stroke-35");var subQ43=sQuery(id+"F0.wireOp",EDGE,"E4.sketch_text.stroke-34");var subQ44=sQuery(id+"F0.wireOp",EDGE,"E4.sketch_text.stroke-33");var subQ45=sQuery(id+"F0.wireOp",EDGE,"E4.sketch_text.stroke-32");var subQ46=sQuery(id+"F0.wireOp",EDGE,"E4.sketch_text.stroke-31");var subQ47=sQuery(id+"F0.wireOp",EDGE,"E4.sketch_text.stroke-30");var subQ48=sQuery(id+"F0.wireOp",EDGE,"E4.sketch_text.stroke-29");var subQ49=sQuery(id+"F0.wireOp",EDGE,"E4.sketch_text.stroke-28");var subQ50=sQuery(id+"F0.wireOp",EDGE,"E4.sketch_text.stroke-27");var subQ51=sQuery(id+"F0.wireOp",EDGE,"E4.sketch_text.stroke-26");var subQ52=sQuery(id+"F0.wireOp",EDGE,"E4.sketch_text.stroke-25");var subQ53=sQuery(id+"F0.wireOp",EDGE,"E4.sketch_text.stroke-24");var subQ54=sQuery(id+"F0.wireOp",EDGE,"E4.sketch_text.stroke-23");var subQ55=sQuery(id+"F0.wireOp",EDGE,"E4.sketch_text.stroke-22");var subQ56=sQuery(id+"F0.wireOp",EDGE,"E4.sketch_text.stroke-21");var subQ57=sQuery(id+"F0.wireOp",EDGE,"E4.sketch_text.stroke-20");var subQ58=sQuery(id+"F0.wireOp",EDGE,"E4.sketch_text.stroke-19");var subQ59=sQuery(id+"F0.wireOp",EDGE,"E4.sketch_text.stroke-18");var subQ60=sQuery(id+"F0.wireOp",EDGE,"E4.sketch_text.stroke-17");var subQ61=sQuery(id+"F0.wireOp",EDGE,"E4.sketch_text.stroke-16");var subQ62=sQuery(id+"F0.wireOp",EDGE,"E4.sketch_text.stroke-15");var subQ63=sQuery(id+"F0.wireOp",EDGE,"E4.sketch_text.stroke-14");var subQ64=sQuery(id+"F0.wireOp",EDGE,"E4.sketch_text.stroke-13");var subQ65=sQuery(id+"F0.wireOp",EDGE,"E4.sketch_text.stroke-12");var subQ66=sQuery(id+"F0.wireOp",EDGE,"E4.sketch_text.stroke-11");var subQ67=sQuery(id+"F0.wireOp",EDGE,"E4.sketch_text.stroke-10");var subQ68=sQuery(id+"F0.wireOp",EDGE,"E4.sketch_text.stroke-9");var subQ69=sQuery(id+"F0.wireOp",EDGE,"E4.sketch_text.stroke-8");var subQ70=sQuery(id+"F0.wireOp",EDGE,"E4.sketch_text.stroke-7");var subQ71=sQuery(id+"F0.wireOp",EDGE,"E4.sketch_text.stroke-6");var subQ72=sQuery(id+"F0.wireOp",EDGE,"E4.sketch_text.stroke-5");var subQ73=sQuery(id+"F0.wireOp",EDGE,"E4.sketch_text.stroke-4");var subQ74=sQuery(id+"F0.wireOp",EDGE,"E4.sketch_text.stroke-3");var subQ75=sQuery(id+"F0.wireOp",EDGE,"E4.sketch_text.stroke-2");var subQ76=sQuery(id+"F0.wireOp",EDGE,"E3.sketch_text.stroke-51");var subQ77=sQuery(id+"F0.wireOp",EDGE,"E3.sketch_text.stroke-53");var subQ78=sQuery(id+"F0.wireOp",EDGE,"E3.sketch_text.stroke-33");var subQ79=sQuery(id+"F0.wireOp",EDGE,"E3.sketch_text.stroke-52");var subQ80=sQuery(id+"F0.wireOp",EDGE,"E3.sketch_text.stroke-32");var subQ81=sQuery(id+"F0.wireOp",EDGE,"E3.sketch_text.stroke-31");var subQ82=sQuery(id+"F0.wireOp",EDGE,"E3.sketch_text.stroke-50");var subQ83=sQuery(id+"F0.wireOp",EDGE,"E3.sketch_text.stroke-30");var subQ84=sQuery(id+"F0.wireOp",EDGE,"E3.sketch_text.stroke-49");var subQ85=sQuery(id+"F0.wireOp",EDGE,"E3.sketch_text.stroke-29");var subQ86=sQuery(id+"F0.wireOp",EDGE,"E3.sketch_text.stroke-48");var subQ87=sQuery(id+"F0.wireOp",EDGE,"E3.sketch_text.stroke-28");var subQ88=sQuery(id+"F0.wireOp",EDGE,"E3.sketch_text.stroke-47");var subQ89=sQuery(id+"F0.wireOp",EDGE,"E3.sketch_text.stroke-27");var subQ90=sQuery(id+"F0.wireOp",EDGE,"E3.sketch_text.stroke-46");var subQ91=sQuery(id+"F0.wireOp",EDGE,"E3.sketch_text.stroke-26");var subQ92=sQuery(id+"F0.wireOp",EDGE,"E3.sketch_text.stroke-45");var subQ93=sQuery(id+"F0.wireOp",EDGE,"E3.sketch_text.stroke-25");var subQ94=sQuery(id+"F0.wireOp",EDGE,"E3.sketch_text.stroke-44");var subQ95=sQuery(id+"F0.wireOp",EDGE,"E3.sketch_text.stroke-24");var subQ96=sQuery(id+"F0.wireOp",EDGE,"E3.sketch_text.stroke-43");var subQ97=sQuery(id+"F0.wireOp",EDGE,"E3.sketch_text.stroke-23");var subQ98=sQuery(id+"F0.wireOp",EDGE,"E3.sketch_text.stroke-42");var subQ99=sQuery(id+"F0.wireOp",EDGE,"E3.sketch_text.stroke-22");var subQ100=sQuery(id+"F0.wireOp",EDGE,"E4.sketch_text.stroke-89");var subQ101=sQuery(id+"F0.wireOp",EDGE,"E3.sketch_text.stroke-4");var subQ102=sQuery(id+"F0.wireOp",EDGE,"E3.sketch_text.stroke-95");var subQ103=sQuery(id+"F0.wireOp",EDGE,"E4.sketch_text.stroke-88");var subQ104=sQuery(id+"F0.wireOp",EDGE,"E3.sketch_text.stroke-3");var subQ105=sQuery(id+"F0.wireOp",EDGE,"E3.sketch_text.stroke-94");var subQ106=sQuery(id+"F0.wireOp",EDGE,"E4.sketch_text.stroke-87");var subQ107=sQuery(id+"F0.wireOp",EDGE,"E3.sketch_text.stroke-2");var subQ108=sQuery(id+"F0.wireOp",EDGE,"E3.sketch_text.stroke-93");var subQ109=sQuery(id+"F0.wireOp",EDGE,"E4.sketch_text.stroke-86");var subQ110=sQuery(id+"F0.wireOp",EDGE,"E3.sketch_text.stroke-1");var subQ111=sQuery(id+"F0.wireOp",EDGE,"E3.sketch_text.stroke-92");var subQ112=sQuery(id+"F0.wireOp",EDGE,"E3.sketch_text.stroke-65");var subQ113=sQuery(id+"F0.wireOp",EDGE,"E4.sketch_text.stroke-85");var subQ114=sQuery(id+"F0.wireOp",EDGE,"E3.sketch_text.stroke-0");var subQ115=sQuery(id+"F0.wireOp",EDGE,"E3.sketch_text.stroke-91");var subQ116=sQuery(id+"F0.wireOp",EDGE,"E3.sketch_text.stroke-21");var subQ117=sQuery(id+"F0.wireOp",EDGE,"E3.sketch_text.stroke-5");var subQ118=sQuery(id+"F0.wireOp",EDGE,"E3.sketch_text.stroke-96");var subQ119=sQuery(id+"F0.wireOp",EDGE,"E4.sketch_text.stroke-79");var subQ120=sQuery(id+"F0.wireOp",EDGE,"E0.bottom");var subQ121=sQuery(id+"F0.wireOp",EDGE,"E3.sketch_text.stroke-85");var subQ122=sQuery(id+"F0.wireOp",EDGE,"E3.sketch_text.stroke-15");var subQ123=sQuery(id+"F0.wireOp",EDGE,"E3.sketch_text.stroke-64");var subQ124=sQuery(id+"F0.wireOp",EDGE,"E4.sketch_text.stroke-84");var subQ125=sQuery(id+"F0.wireOp",EDGE,"E0.right");var subQ126=sQuery(id+"F0.wireOp",EDGE,"E3.sketch_text.stroke-90");var subQ127=sQuery(id+"F0.wireOp",EDGE,"E3.sketch_text.stroke-20");var subQ128=sQuery(id+"F0.wireOp",EDGE,"E3.sketch_text.stroke-62");var subQ129=sQuery(id+"F0.wireOp",EDGE,"E3.sketch_text.stroke-40");var subQ130=sQuery(id+"F0.wireOp",EDGE,"E4.sketch_text.stroke-82");var subQ131=sQuery(id+"F0.wireOp",EDGE,"E0.top");var subQ132=sQuery(id+"F0.wireOp",EDGE,"E3.sketch_text.stroke-88");var subQ133=sQuery(id+"F0.wireOp",EDGE,"E3.sketch_text.stroke-18");var subQ134=sQuery(id+"F0.wireOp",EDGE,"E3.sketch_text.stroke-63");var subQ135=sQuery(id+"F0.wireOp",EDGE,"E3.sketch_text.stroke-41");var subQ136=sQuery(id+"F0.wireOp",EDGE,"E4.sketch_text.stroke-83");var subQ137=sQuery(id+"F0.wireOp",EDGE,"E0.left");var subQ138=sQuery(id+"F0.wireOp",EDGE,"E3.sketch_text.stroke-89");var subQ139=sQuery(id+"F0.wireOp",EDGE,"E3.sketch_text.stroke-19");var subQ140=sQuery(id+"F0.wireOp",EDGE,"E3.sketch_text.stroke-6");var subQ141=sQuery(id+"F0.wireOp",EDGE,"E3.sketch_text.stroke-97");var subQ142=sQuery(id+"F0.wireOp",EDGE,"E3.sketch_text.stroke-7");var subQ143=sQuery(id+"F0.wireOp",EDGE,"E3.sketch_text.stroke-98");var subQ144=sQuery(id+"F0.wireOp",EDGE,"E3.sketch_text.stroke-12");var subQ145=sQuery(id+"F0.wireOp",EDGE,"E3.sketch_text.stroke-105");var subQ146=sQuery(id+"F0.wireOp",EDGE,"E3.sketch_text.stroke-13");var subQ147=sQuery(id+"F0.wireOp",EDGE,"E4.sketch_text.stroke-0");var subQ148=sQuery(id+"F0.wireOp",EDGE,"E3.sketch_text.stroke-14");var subQ149=sQuery(id+"F0.wireOp",EDGE,"E4.sketch_text.stroke-1");var subQ150=sQuery(id+"F0.wireOp",EDGE,"E3.sketch_text.stroke-16");var subQ151=sQuery(id+"F0.wireOp",EDGE,"E3.sketch_text.stroke-17");var subQ152=sQuery(id+"F0.wireOp",EDGE,"E3.sketch_text.stroke-55");var subQ153=sQuery(id+"F0.wireOp",EDGE,"E3.sketch_text.stroke-56");var subQ154=sQuery(id+"F0.wireOp",EDGE,"E3.sketch_text.stroke-57");var subQ155=sQuery(id+"F0.wireOp",EDGE,"E3.sketch_text.stroke-58");var subQ156=sQuery(id+"F0.wireOp",EDGE,"E3.sketch_text.stroke-59");var subQ157=sQuery(id+"F0.wireOp",EDGE,"E3.sketch_text.stroke-60");var subQ158=sQuery(id+"F0.wireOp",EDGE,"E3.sketch_text.stroke-61");var subQ159=sQuery(id+"F0.wireOp",EDGE,"E3.sketch_text.stroke-66");var subQ160=sQuery(id+"F0.wireOp",EDGE,"E3.sketch_text.stroke-67");var subQ161=sQuery(id+"F0.wireOp",EDGE,"E3.sketch_text.stroke-68");var subQ162=sQuery(id+"F0.wireOp",EDGE,"E3.sketch_text.stroke-69");var subQ163=sQuery(id+"F0.wireOp",EDGE,"E3.sketch_text.stroke-70");var subQ164=sQuery(id+"F0.wireOp",EDGE,"E3.sketch_text.stroke-71");var subQ165=sQuery(id+"F0.wireOp",EDGE,"E3.sketch_text.stroke-78");var subQ166=sQuery(id+"F0.wireOp",EDGE,"E3.sketch_text.stroke-79");var subQ167=sQuery(id+"F0.wireOp",EDGE,"E3.sketch_text.stroke-80");var subQ168=sQuery(id+"F0.wireOp",EDGE,"E3.sketch_text.stroke-81");var subQ169=sQuery(id+"F0.wireOp",EDGE,"E3.sketch_text.stroke-82");var subQ170=sQuery(id+"F0.wireOp",EDGE,"E3.sketch_text.stroke-83");var subQ171=sQuery(id+"F0.wireOp",EDGE,"E3.sketch_text.stroke-84");var subQ172=sQuery(id+"F0.wireOp",EDGE,"E3.sketch_text.stroke-86");var subQ173=sQuery(id+"F0.wireOp",EDGE,"E3.sketch_text.stroke-87");var subQ174=sQuery(id+"F0.wireOp",EDGE,"E3.sketch_text.stroke-99");var subQ175=sQuery(id+"F0.wireOp",EDGE,"E3.sketch_text.stroke-100");var subQ176=sQuery(id+"F0.wireOp",EDGE,"E3.sketch_text.stroke-101");var subQ177=sQuery(id+"F0.wireOp",EDGE,"E3.sketch_text.stroke-102");var subQ178=sQuery(id+"F0.wireOp",EDGE,"E3.sketch_text.stroke-103");var subQ179=sQuery(id+"F0.wireOp",EDGE,"E3.sketch_text.stroke-104");Q0=makeQuery(id+"F6.opFillet","BLEND_EDGE",EDGE,{"blendedFrom":[makeQuery(id+"F3.opExtrude","CAP_EDGE",EDGE,{"disambiguationData":[OSD([subQ125])],"isStart":false}),makeQuery(id+"F5.boolean.opBoolean","SPLIT",FACE,{"disambiguationData":[TD([makeQuery(id+"F3.opExtrude","SWEPT_FACE",FACE,{"disambiguationData":[OSD([subQ120])]})])],"derivedFrom":makeQuery(id+"F3.opExtrude","CAP_FACE",FACE,{"disambiguationData":[OSD([subQ120,subQ131,subQ137,subQ125,subQ114,subQ110,subQ107,subQ104,subQ101,subQ117,subQ140,subQ142,subQ144,subQ146,subQ148,subQ122,subQ150,subQ151,subQ133,subQ139,subQ127,subQ116,subQ99,subQ97,subQ95,subQ93,subQ91,subQ89,subQ87,subQ85,subQ83,subQ81,subQ80,subQ78,subQ129,subQ135,subQ98,subQ96,subQ94,subQ92,subQ90,subQ88,subQ86,subQ84,subQ82,subQ76,subQ79,subQ77,subQ0,subQ152,subQ153,subQ154,subQ155,subQ156,subQ157,subQ158,subQ128,subQ134,subQ123,subQ112,subQ159,subQ160,subQ161,subQ162,subQ163,subQ164,subQ165,subQ166,subQ167,subQ168,subQ169,subQ170,subQ171,subQ121,subQ172,subQ173,subQ132,subQ138,subQ126,subQ115,subQ111,subQ108,subQ105,subQ102,subQ118,subQ141,subQ143,subQ174,subQ175,subQ176,subQ177,subQ178,subQ179,subQ145,subQ147,subQ149,subQ75,subQ74,subQ73,subQ72,subQ71,subQ70,subQ69,subQ68,subQ67,subQ66,subQ65,subQ64,subQ63,subQ62,subQ61,subQ60,subQ59,subQ58,subQ57,subQ56,subQ55,subQ54,subQ53,subQ52,subQ51,subQ50,subQ49,subQ48,subQ47,subQ46,subQ45,subQ44,subQ43,subQ42,subQ41,subQ40,subQ39,subQ38,subQ37,subQ36,subQ35,subQ34,subQ33,subQ32,subQ31,subQ30,subQ29,subQ28,subQ27,subQ26,subQ25,subQ24,subQ23,subQ22,subQ21,subQ20,subQ19,subQ18,subQ17,subQ16,subQ15,subQ14,subQ13,subQ12,subQ11,subQ10,subQ9,subQ8,subQ7,subQ6,subQ5,subQ4,subQ3,subQ119,subQ2,subQ1,subQ130,subQ136,subQ124,subQ113,subQ109,subQ106,subQ103,subQ100])],"isStart":false})})],"blendedInto":[makeQuery(id+"F5.boolean.opBoolean","SPLIT",FACE,{"disambiguationData":[TD([makeQuery(id+"F3.opExtrude","SWEPT_FACE",FACE,{"disambiguationData":[OSD([subQ120])]})])],"derivedFrom":makeQuery(id+"F3.opExtrude","CAP_FACE",FACE,{"disambiguationData":[OSD([subQ120,subQ131,subQ137,subQ125,subQ114,subQ110,subQ107,subQ104,subQ101,subQ117,subQ140,subQ142,subQ144,subQ146,subQ148,subQ122,subQ150,subQ151,subQ133,subQ139,subQ127,subQ116,subQ99,subQ97,subQ95,subQ93,subQ91,subQ89,subQ87,subQ85,subQ83,subQ81,subQ80,subQ78,subQ129,subQ135,subQ98,subQ96,subQ94,subQ92,subQ90,subQ88,subQ86,subQ84,subQ82,subQ76,subQ79,subQ77,subQ0,subQ152,subQ153,subQ154,subQ155,subQ156,subQ157,subQ158,subQ128,subQ134,subQ123,subQ112,subQ159,subQ160,subQ161,subQ162,subQ163,subQ164,subQ165,subQ166,subQ167,subQ168,subQ169,subQ170,subQ171,subQ121,subQ172,subQ173,subQ132,subQ138,subQ126,subQ115,subQ111,subQ108,subQ105,subQ102,subQ118,subQ141,subQ143,subQ174,subQ175,subQ176,subQ177,subQ178,subQ179,subQ145,subQ147,subQ149,subQ75,subQ74,subQ73,subQ72,subQ71,subQ70,subQ69,subQ68,subQ67,subQ66,subQ65,subQ64,subQ63,subQ62,subQ61,subQ60,subQ59,subQ58,subQ57,subQ56,subQ55,subQ54,subQ53,subQ52,subQ51,subQ50,subQ49,subQ48,subQ47,subQ46,subQ45,subQ44,subQ43,subQ42,subQ41,subQ40,subQ39,subQ38,subQ37,subQ36,subQ35,subQ34,subQ33,subQ32,subQ31,subQ30,subQ29,subQ28,subQ27,subQ26,subQ25,subQ24,subQ23,subQ22,subQ21,subQ20,subQ19,subQ18,subQ17,subQ16,subQ15,subQ14,subQ13,subQ12,subQ11,subQ10,subQ9,subQ8,subQ7,subQ6,subQ5,subQ4,subQ3,subQ119,subQ2,subQ1,subQ130,subQ136,subQ124,subQ113,subQ109,subQ106,subQ103,subQ100])],"isStart":false})})]});}
            var Q1;
            {var subQ0=sQuery(id+"F0.wireOp",EDGE,"E3.sketch_text.stroke-54");var subQ1=sQuery(id+"F0.wireOp",EDGE,"E4.sketch_text.stroke-81");var subQ2=sQuery(id+"F0.wireOp",EDGE,"E4.sketch_text.stroke-80");var subQ3=sQuery(id+"F0.wireOp",EDGE,"E4.sketch_text.stroke-78");var subQ4=sQuery(id+"F0.wireOp",EDGE,"E4.sketch_text.stroke-77");var subQ5=sQuery(id+"F0.wireOp",EDGE,"E4.sketch_text.stroke-76");var subQ6=sQuery(id+"F0.wireOp",EDGE,"E4.sketch_text.stroke-75");var subQ7=sQuery(id+"F0.wireOp",EDGE,"E4.sketch_text.stroke-74");var subQ8=sQuery(id+"F0.wireOp",EDGE,"E4.sketch_text.stroke-73");var subQ9=sQuery(id+"F0.wireOp",EDGE,"E4.sketch_text.stroke-72");var subQ10=sQuery(id+"F0.wireOp",EDGE,"E4.sketch_text.stroke-71");var subQ11=sQuery(id+"F0.wireOp",EDGE,"E4.sketch_text.stroke-70");var subQ12=sQuery(id+"F0.wireOp",EDGE,"E4.sketch_text.stroke-69");var subQ13=sQuery(id+"F0.wireOp",EDGE,"E4.sketch_text.stroke-68");var subQ14=sQuery(id+"F0.wireOp",EDGE,"E4.sketch_text.stroke-67");var subQ15=sQuery(id+"F0.wireOp",EDGE,"E4.sketch_text.stroke-66");var subQ16=sQuery(id+"F0.wireOp",EDGE,"E4.sketch_text.stroke-65");var subQ17=sQuery(id+"F0.wireOp",EDGE,"E4.sketch_text.stroke-64");var subQ18=sQuery(id+"F0.wireOp",EDGE,"E4.sketch_text.stroke-63");var subQ19=sQuery(id+"F0.wireOp",EDGE,"E4.sketch_text.stroke-62");var subQ20=sQuery(id+"F0.wireOp",EDGE,"E4.sketch_text.stroke-61");var subQ21=sQuery(id+"F0.wireOp",EDGE,"E4.sketch_text.stroke-60");var subQ22=sQuery(id+"F0.wireOp",EDGE,"E4.sketch_text.stroke-59");var subQ23=sQuery(id+"F0.wireOp",EDGE,"E4.sketch_text.stroke-58");var subQ24=sQuery(id+"F0.wireOp",EDGE,"E4.sketch_text.stroke-57");var subQ25=sQuery(id+"F0.wireOp",EDGE,"E4.sketch_text.stroke-56");var subQ26=sQuery(id+"F0.wireOp",EDGE,"E4.sketch_text.stroke-55");var subQ27=sQuery(id+"F0.wireOp",EDGE,"E4.sketch_text.stroke-54");var subQ28=sQuery(id+"F0.wireOp",EDGE,"E4.sketch_text.stroke-53");var subQ29=sQuery(id+"F0.wireOp",EDGE,"E4.sketch_text.stroke-52");var subQ30=sQuery(id+"F0.wireOp",EDGE,"E4.sketch_text.stroke-51");var subQ31=sQuery(id+"F0.wireOp",EDGE,"E4.sketch_text.stroke-50");var subQ32=sQuery(id+"F0.wireOp",EDGE,"E4.sketch_text.stroke-49");var subQ33=sQuery(id+"F0.wireOp",EDGE,"E4.sketch_text.stroke-48");var subQ34=sQuery(id+"F0.wireOp",EDGE,"E4.sketch_text.stroke-47");var subQ35=sQuery(id+"F0.wireOp",EDGE,"E4.sketch_text.stroke-46");var subQ36=sQuery(id+"F0.wireOp",EDGE,"E4.sketch_text.stroke-41");var subQ37=sQuery(id+"F0.wireOp",EDGE,"E4.sketch_text.stroke-40");var subQ38=sQuery(id+"F0.wireOp",EDGE,"E4.sketch_text.stroke-39");var subQ39=sQuery(id+"F0.wireOp",EDGE,"E4.sketch_text.stroke-38");var subQ40=sQuery(id+"F0.wireOp",EDGE,"E4.sketch_text.stroke-37");var subQ41=sQuery(id+"F0.wireOp",EDGE,"E4.sketch_text.stroke-36");var subQ42=sQuery(id+"F0.wireOp",EDGE,"E4.sketch_text.stroke-35");var subQ43=sQuery(id+"F0.wireOp",EDGE,"E4.sketch_text.stroke-34");var subQ44=sQuery(id+"F0.wireOp",EDGE,"E4.sketch_text.stroke-33");var subQ45=sQuery(id+"F0.wireOp",EDGE,"E4.sketch_text.stroke-32");var subQ46=sQuery(id+"F0.wireOp",EDGE,"E4.sketch_text.stroke-31");var subQ47=sQuery(id+"F0.wireOp",EDGE,"E4.sketch_text.stroke-30");var subQ48=sQuery(id+"F0.wireOp",EDGE,"E4.sketch_text.stroke-29");var subQ49=sQuery(id+"F0.wireOp",EDGE,"E4.sketch_text.stroke-28");var subQ50=sQuery(id+"F0.wireOp",EDGE,"E4.sketch_text.stroke-27");var subQ51=sQuery(id+"F0.wireOp",EDGE,"E4.sketch_text.stroke-26");var subQ52=sQuery(id+"F0.wireOp",EDGE,"E4.sketch_text.stroke-25");var subQ53=sQuery(id+"F0.wireOp",EDGE,"E4.sketch_text.stroke-24");var subQ54=sQuery(id+"F0.wireOp",EDGE,"E4.sketch_text.stroke-23");var subQ55=sQuery(id+"F0.wireOp",EDGE,"E4.sketch_text.stroke-22");var subQ56=sQuery(id+"F0.wireOp",EDGE,"E4.sketch_text.stroke-21");var subQ57=sQuery(id+"F0.wireOp",EDGE,"E4.sketch_text.stroke-20");var subQ58=sQuery(id+"F0.wireOp",EDGE,"E4.sketch_text.stroke-19");var subQ59=sQuery(id+"F0.wireOp",EDGE,"E4.sketch_text.stroke-18");var subQ60=sQuery(id+"F0.wireOp",EDGE,"E4.sketch_text.stroke-17");var subQ61=sQuery(id+"F0.wireOp",EDGE,"E4.sketch_text.stroke-16");var subQ62=sQuery(id+"F0.wireOp",EDGE,"E4.sketch_text.stroke-15");var subQ63=sQuery(id+"F0.wireOp",EDGE,"E4.sketch_text.stroke-14");var subQ64=sQuery(id+"F0.wireOp",EDGE,"E4.sketch_text.stroke-13");var subQ65=sQuery(id+"F0.wireOp",EDGE,"E4.sketch_text.stroke-12");var subQ66=sQuery(id+"F0.wireOp",EDGE,"E4.sketch_text.stroke-11");var subQ67=sQuery(id+"F0.wireOp",EDGE,"E4.sketch_text.stroke-10");var subQ68=sQuery(id+"F0.wireOp",EDGE,"E4.sketch_text.stroke-9");var subQ69=sQuery(id+"F0.wireOp",EDGE,"E4.sketch_text.stroke-8");var subQ70=sQuery(id+"F0.wireOp",EDGE,"E4.sketch_text.stroke-7");var subQ71=sQuery(id+"F0.wireOp",EDGE,"E4.sketch_text.stroke-6");var subQ72=sQuery(id+"F0.wireOp",EDGE,"E4.sketch_text.stroke-5");var subQ73=sQuery(id+"F0.wireOp",EDGE,"E4.sketch_text.stroke-4");var subQ74=sQuery(id+"F0.wireOp",EDGE,"E4.sketch_text.stroke-3");var subQ75=sQuery(id+"F0.wireOp",EDGE,"E4.sketch_text.stroke-2");var subQ76=sQuery(id+"F0.wireOp",EDGE,"E3.sketch_text.stroke-51");var subQ77=sQuery(id+"F0.wireOp",EDGE,"E3.sketch_text.stroke-53");var subQ78=sQuery(id+"F0.wireOp",EDGE,"E3.sketch_text.stroke-33");var subQ79=sQuery(id+"F0.wireOp",EDGE,"E3.sketch_text.stroke-52");var subQ80=sQuery(id+"F0.wireOp",EDGE,"E3.sketch_text.stroke-32");var subQ81=sQuery(id+"F0.wireOp",EDGE,"E3.sketch_text.stroke-31");var subQ82=sQuery(id+"F0.wireOp",EDGE,"E3.sketch_text.stroke-50");var subQ83=sQuery(id+"F0.wireOp",EDGE,"E3.sketch_text.stroke-30");var subQ84=sQuery(id+"F0.wireOp",EDGE,"E3.sketch_text.stroke-49");var subQ85=sQuery(id+"F0.wireOp",EDGE,"E3.sketch_text.stroke-29");var subQ86=sQuery(id+"F0.wireOp",EDGE,"E3.sketch_text.stroke-48");var subQ87=sQuery(id+"F0.wireOp",EDGE,"E3.sketch_text.stroke-28");var subQ88=sQuery(id+"F0.wireOp",EDGE,"E3.sketch_text.stroke-47");var subQ89=sQuery(id+"F0.wireOp",EDGE,"E3.sketch_text.stroke-27");var subQ90=sQuery(id+"F0.wireOp",EDGE,"E3.sketch_text.stroke-46");var subQ91=sQuery(id+"F0.wireOp",EDGE,"E3.sketch_text.stroke-26");var subQ92=sQuery(id+"F0.wireOp",EDGE,"E3.sketch_text.stroke-45");var subQ93=sQuery(id+"F0.wireOp",EDGE,"E3.sketch_text.stroke-25");var subQ94=sQuery(id+"F0.wireOp",EDGE,"E3.sketch_text.stroke-44");var subQ95=sQuery(id+"F0.wireOp",EDGE,"E3.sketch_text.stroke-24");var subQ96=sQuery(id+"F0.wireOp",EDGE,"E3.sketch_text.stroke-43");var subQ97=sQuery(id+"F0.wireOp",EDGE,"E3.sketch_text.stroke-23");var subQ98=sQuery(id+"F0.wireOp",EDGE,"E3.sketch_text.stroke-42");var subQ99=sQuery(id+"F0.wireOp",EDGE,"E3.sketch_text.stroke-22");var subQ100=sQuery(id+"F0.wireOp",EDGE,"E4.sketch_text.stroke-89");var subQ101=sQuery(id+"F0.wireOp",EDGE,"E3.sketch_text.stroke-4");var subQ102=sQuery(id+"F0.wireOp",EDGE,"E3.sketch_text.stroke-95");var subQ103=sQuery(id+"F0.wireOp",EDGE,"E4.sketch_text.stroke-88");var subQ104=sQuery(id+"F0.wireOp",EDGE,"E3.sketch_text.stroke-3");var subQ105=sQuery(id+"F0.wireOp",EDGE,"E3.sketch_text.stroke-94");var subQ106=sQuery(id+"F0.wireOp",EDGE,"E4.sketch_text.stroke-87");var subQ107=sQuery(id+"F0.wireOp",EDGE,"E3.sketch_text.stroke-2");var subQ108=sQuery(id+"F0.wireOp",EDGE,"E3.sketch_text.stroke-93");var subQ109=sQuery(id+"F0.wireOp",EDGE,"E4.sketch_text.stroke-86");var subQ110=sQuery(id+"F0.wireOp",EDGE,"E3.sketch_text.stroke-1");var subQ111=sQuery(id+"F0.wireOp",EDGE,"E3.sketch_text.stroke-92");var subQ112=sQuery(id+"F0.wireOp",EDGE,"E3.sketch_text.stroke-65");var subQ113=sQuery(id+"F0.wireOp",EDGE,"E4.sketch_text.stroke-85");var subQ114=sQuery(id+"F0.wireOp",EDGE,"E3.sketch_text.stroke-0");var subQ115=sQuery(id+"F0.wireOp",EDGE,"E3.sketch_text.stroke-91");var subQ116=sQuery(id+"F0.wireOp",EDGE,"E3.sketch_text.stroke-21");var subQ117=sQuery(id+"F0.wireOp",EDGE,"E3.sketch_text.stroke-5");var subQ118=sQuery(id+"F0.wireOp",EDGE,"E3.sketch_text.stroke-96");var subQ119=sQuery(id+"F0.wireOp",EDGE,"E4.sketch_text.stroke-79");var subQ120=sQuery(id+"F0.wireOp",EDGE,"E0.bottom");var subQ121=sQuery(id+"F0.wireOp",EDGE,"E3.sketch_text.stroke-85");var subQ122=sQuery(id+"F0.wireOp",EDGE,"E3.sketch_text.stroke-15");var subQ123=sQuery(id+"F0.wireOp",EDGE,"E3.sketch_text.stroke-64");var subQ124=sQuery(id+"F0.wireOp",EDGE,"E4.sketch_text.stroke-84");var subQ125=sQuery(id+"F0.wireOp",EDGE,"E0.right");var subQ126=sQuery(id+"F0.wireOp",EDGE,"E3.sketch_text.stroke-90");var subQ127=sQuery(id+"F0.wireOp",EDGE,"E3.sketch_text.stroke-20");var subQ128=sQuery(id+"F0.wireOp",EDGE,"E3.sketch_text.stroke-62");var subQ129=sQuery(id+"F0.wireOp",EDGE,"E3.sketch_text.stroke-40");var subQ130=sQuery(id+"F0.wireOp",EDGE,"E4.sketch_text.stroke-82");var subQ131=sQuery(id+"F0.wireOp",EDGE,"E0.top");var subQ132=sQuery(id+"F0.wireOp",EDGE,"E3.sketch_text.stroke-88");var subQ133=sQuery(id+"F0.wireOp",EDGE,"E3.sketch_text.stroke-18");var subQ134=sQuery(id+"F0.wireOp",EDGE,"E3.sketch_text.stroke-63");var subQ135=sQuery(id+"F0.wireOp",EDGE,"E3.sketch_text.stroke-41");var subQ136=sQuery(id+"F0.wireOp",EDGE,"E4.sketch_text.stroke-83");var subQ137=sQuery(id+"F0.wireOp",EDGE,"E0.left");var subQ138=sQuery(id+"F0.wireOp",EDGE,"E3.sketch_text.stroke-89");var subQ139=sQuery(id+"F0.wireOp",EDGE,"E3.sketch_text.stroke-19");var subQ140=sQuery(id+"F0.wireOp",EDGE,"E3.sketch_text.stroke-6");var subQ141=sQuery(id+"F0.wireOp",EDGE,"E3.sketch_text.stroke-97");var subQ142=sQuery(id+"F0.wireOp",EDGE,"E3.sketch_text.stroke-7");var subQ143=sQuery(id+"F0.wireOp",EDGE,"E3.sketch_text.stroke-98");var subQ144=sQuery(id+"F0.wireOp",EDGE,"E3.sketch_text.stroke-12");var subQ145=sQuery(id+"F0.wireOp",EDGE,"E3.sketch_text.stroke-105");var subQ146=sQuery(id+"F0.wireOp",EDGE,"E3.sketch_text.stroke-13");var subQ147=sQuery(id+"F0.wireOp",EDGE,"E4.sketch_text.stroke-0");var subQ148=sQuery(id+"F0.wireOp",EDGE,"E3.sketch_text.stroke-14");var subQ149=sQuery(id+"F0.wireOp",EDGE,"E4.sketch_text.stroke-1");var subQ150=sQuery(id+"F0.wireOp",EDGE,"E3.sketch_text.stroke-16");var subQ151=sQuery(id+"F0.wireOp",EDGE,"E3.sketch_text.stroke-17");var subQ152=sQuery(id+"F0.wireOp",EDGE,"E3.sketch_text.stroke-55");var subQ153=sQuery(id+"F0.wireOp",EDGE,"E3.sketch_text.stroke-56");var subQ154=sQuery(id+"F0.wireOp",EDGE,"E3.sketch_text.stroke-57");var subQ155=sQuery(id+"F0.wireOp",EDGE,"E3.sketch_text.stroke-58");var subQ156=sQuery(id+"F0.wireOp",EDGE,"E3.sketch_text.stroke-59");var subQ157=sQuery(id+"F0.wireOp",EDGE,"E3.sketch_text.stroke-60");var subQ158=sQuery(id+"F0.wireOp",EDGE,"E3.sketch_text.stroke-61");var subQ159=sQuery(id+"F0.wireOp",EDGE,"E3.sketch_text.stroke-66");var subQ160=sQuery(id+"F0.wireOp",EDGE,"E3.sketch_text.stroke-67");var subQ161=sQuery(id+"F0.wireOp",EDGE,"E3.sketch_text.stroke-68");var subQ162=sQuery(id+"F0.wireOp",EDGE,"E3.sketch_text.stroke-69");var subQ163=sQuery(id+"F0.wireOp",EDGE,"E3.sketch_text.stroke-70");var subQ164=sQuery(id+"F0.wireOp",EDGE,"E3.sketch_text.stroke-71");var subQ165=sQuery(id+"F0.wireOp",EDGE,"E3.sketch_text.stroke-78");var subQ166=sQuery(id+"F0.wireOp",EDGE,"E3.sketch_text.stroke-79");var subQ167=sQuery(id+"F0.wireOp",EDGE,"E3.sketch_text.stroke-80");var subQ168=sQuery(id+"F0.wireOp",EDGE,"E3.sketch_text.stroke-81");var subQ169=sQuery(id+"F0.wireOp",EDGE,"E3.sketch_text.stroke-82");var subQ170=sQuery(id+"F0.wireOp",EDGE,"E3.sketch_text.stroke-83");var subQ171=sQuery(id+"F0.wireOp",EDGE,"E3.sketch_text.stroke-84");var subQ172=sQuery(id+"F0.wireOp",EDGE,"E3.sketch_text.stroke-86");var subQ173=sQuery(id+"F0.wireOp",EDGE,"E3.sketch_text.stroke-87");var subQ174=sQuery(id+"F0.wireOp",EDGE,"E3.sketch_text.stroke-99");var subQ175=sQuery(id+"F0.wireOp",EDGE,"E3.sketch_text.stroke-100");var subQ176=sQuery(id+"F0.wireOp",EDGE,"E3.sketch_text.stroke-101");var subQ177=sQuery(id+"F0.wireOp",EDGE,"E3.sketch_text.stroke-102");var subQ178=sQuery(id+"F0.wireOp",EDGE,"E3.sketch_text.stroke-103");var subQ179=sQuery(id+"F0.wireOp",EDGE,"E3.sketch_text.stroke-104");Q1=makeQuery(id+"F6.opFillet","BLEND_EDGE",EDGE,{"blendedFrom":[makeQuery(id+"F3.opExtrude","CAP_EDGE",EDGE,{"disambiguationData":[OSD([subQ131])],"isStart":false}),makeQuery(id+"F5.boolean.opBoolean","SPLIT",FACE,{"disambiguationData":[TD([makeQuery(id+"F3.opExtrude","SWEPT_FACE",FACE,{"disambiguationData":[OSD([subQ120])]})])],"derivedFrom":makeQuery(id+"F3.opExtrude","CAP_FACE",FACE,{"disambiguationData":[OSD([subQ120,subQ131,subQ137,subQ125,subQ114,subQ110,subQ107,subQ104,subQ101,subQ117,subQ140,subQ142,subQ144,subQ146,subQ148,subQ122,subQ150,subQ151,subQ133,subQ139,subQ127,subQ116,subQ99,subQ97,subQ95,subQ93,subQ91,subQ89,subQ87,subQ85,subQ83,subQ81,subQ80,subQ78,subQ129,subQ135,subQ98,subQ96,subQ94,subQ92,subQ90,subQ88,subQ86,subQ84,subQ82,subQ76,subQ79,subQ77,subQ0,subQ152,subQ153,subQ154,subQ155,subQ156,subQ157,subQ158,subQ128,subQ134,subQ123,subQ112,subQ159,subQ160,subQ161,subQ162,subQ163,subQ164,subQ165,subQ166,subQ167,subQ168,subQ169,subQ170,subQ171,subQ121,subQ172,subQ173,subQ132,subQ138,subQ126,subQ115,subQ111,subQ108,subQ105,subQ102,subQ118,subQ141,subQ143,subQ174,subQ175,subQ176,subQ177,subQ178,subQ179,subQ145,subQ147,subQ149,subQ75,subQ74,subQ73,subQ72,subQ71,subQ70,subQ69,subQ68,subQ67,subQ66,subQ65,subQ64,subQ63,subQ62,subQ61,subQ60,subQ59,subQ58,subQ57,subQ56,subQ55,subQ54,subQ53,subQ52,subQ51,subQ50,subQ49,subQ48,subQ47,subQ46,subQ45,subQ44,subQ43,subQ42,subQ41,subQ40,subQ39,subQ38,subQ37,subQ36,subQ35,subQ34,subQ33,subQ32,subQ31,subQ30,subQ29,subQ28,subQ27,subQ26,subQ25,subQ24,subQ23,subQ22,subQ21,subQ20,subQ19,subQ18,subQ17,subQ16,subQ15,subQ14,subQ13,subQ12,subQ11,subQ10,subQ9,subQ8,subQ7,subQ6,subQ5,subQ4,subQ3,subQ119,subQ2,subQ1,subQ130,subQ136,subQ124,subQ113,subQ109,subQ106,subQ103,subQ100])],"isStart":false})})],"blendedInto":[makeQuery(id+"F5.boolean.opBoolean","SPLIT",FACE,{"disambiguationData":[TD([makeQuery(id+"F3.opExtrude","SWEPT_FACE",FACE,{"disambiguationData":[OSD([subQ120])]})])],"derivedFrom":makeQuery(id+"F3.opExtrude","CAP_FACE",FACE,{"disambiguationData":[OSD([subQ120,subQ131,subQ137,subQ125,subQ114,subQ110,subQ107,subQ104,subQ101,subQ117,subQ140,subQ142,subQ144,subQ146,subQ148,subQ122,subQ150,subQ151,subQ133,subQ139,subQ127,subQ116,subQ99,subQ97,subQ95,subQ93,subQ91,subQ89,subQ87,subQ85,subQ83,subQ81,subQ80,subQ78,subQ129,subQ135,subQ98,subQ96,subQ94,subQ92,subQ90,subQ88,subQ86,subQ84,subQ82,subQ76,subQ79,subQ77,subQ0,subQ152,subQ153,subQ154,subQ155,subQ156,subQ157,subQ158,subQ128,subQ134,subQ123,subQ112,subQ159,subQ160,subQ161,subQ162,subQ163,subQ164,subQ165,subQ166,subQ167,subQ168,subQ169,subQ170,subQ171,subQ121,subQ172,subQ173,subQ132,subQ138,subQ126,subQ115,subQ111,subQ108,subQ105,subQ102,subQ118,subQ141,subQ143,subQ174,subQ175,subQ176,subQ177,subQ178,subQ179,subQ145,subQ147,subQ149,subQ75,subQ74,subQ73,subQ72,subQ71,subQ70,subQ69,subQ68,subQ67,subQ66,subQ65,subQ64,subQ63,subQ62,subQ61,subQ60,subQ59,subQ58,subQ57,subQ56,subQ55,subQ54,subQ53,subQ52,subQ51,subQ50,subQ49,subQ48,subQ47,subQ46,subQ45,subQ44,subQ43,subQ42,subQ41,subQ40,subQ39,subQ38,subQ37,subQ36,subQ35,subQ34,subQ33,subQ32,subQ31,subQ30,subQ29,subQ28,subQ27,subQ26,subQ25,subQ24,subQ23,subQ22,subQ21,subQ20,subQ19,subQ18,subQ17,subQ16,subQ15,subQ14,subQ13,subQ12,subQ11,subQ10,subQ9,subQ8,subQ7,subQ6,subQ5,subQ4,subQ3,subQ119,subQ2,subQ1,subQ130,subQ136,subQ124,subQ113,subQ109,subQ106,subQ103,subQ100])],"isStart":false})})]});}
            var Q2;
            Q2=makeQuery(id+"F6.opFillet","BLEND_EDGE",EDGE,{"blendedFrom":[makeQuery(id+"F3.opExtrude","CAP_EDGE",EDGE,{"disambiguationData":[OSD([sQuery(id+"F0.wireOp",EDGE,"E0.top")])],"isStart":false}),makeQuery(id+"F3.opExtrude","CAP_EDGE",EDGE,{"disambiguationData":[OSD([sQuery(id+"F0.wireOp",EDGE,"E0.right")])],"isStart":false})],"blendedInto":[]});
            var Q3;
            Q3=makeQuery(id+"F3.opExtrude","SWEPT_EDGE",EDGE,{"disambiguationData":[OSD([sQuery(id+"F0.wireOp",EDGE,"E0.top"),sQuery(id+"F0.wireOp",EDGE,"E0.left")])]});
            fillet(context, id + "F7", {"entities" : qUnion([Q0, Q1, Q2, Q3]), "radius" : 5 * mm, "tangentPropagation" : true, "allowEdgeOverflow" : false});
        }
        {
            var Q0;
            Q0=makeQuery(id+"F3.opExtrude","SWEPT_FACE",FACE,{"disambiguationData":[OSD([sQuery(id+"F0.wireOp",EDGE,"E0.bottom")])]});
            var sketch = newSketch(context, id + "F8", { "sketchPlane" : qUnion([Q0])});
            skText(sketch, "E16", { "text": "NJ 2017", "fontName": "OpenSans-Bold.ttf"});
            skLineSegment(sketch, "E17", {"start": v(-90.13, 0) * mm, "end": v(-90.13, 10) * mm, "construction": true});
            skLineSegment(sketch, "E18", {"start": v(-90.13, 10) * mm, "end": v(-90.13, 5) * mm, "construction": true});
            skLineSegment(sketch, "E19", {"start": v(-90.13, 5) * mm, "end": v(100, 5) * mm, "construction": true});
            skLineSegment(sketch, "E20", {"start": v(100, 5) * mm, "end": v(100, 10) * mm, "construction": true});
            skLineSegment(sketch, "E21", {"start": v(100, 10) * mm, "end": v(100, 0) * mm, "construction": true});
            const initialGuessF8  = {"E16": [0.06255, 0.0025, 1, 0, 0.00628]};
            skSetInitialGuess(sketch, initialGuessF8);
            skSolve(sketch);
        }
        {
            var Q0;
            Q0=makeQuery(id+"F8.imprint","IMPRINT",FACE,{"disambiguationData":[TD([[makeQuery(id+"F8.imprint","IMPRINT",EDGE,{"derivedFrom":sQuery(id+"F8.wireOp",EDGE,"E16.sketch_text.stroke-0")}),-1.0]])]});
            var Q1;
            Q1=makeQuery(id+"F8.imprint","IMPRINT",FACE,{"disambiguationData":[TD([[makeQuery(id+"F8.imprint","IMPRINT",EDGE,{"derivedFrom":sQuery(id+"F8.wireOp",EDGE,"E16.sketch_text.stroke-14")}),-1.0]])]});
            var Q2;
            Q2=makeQuery(id+"F8.imprint","IMPRINT",FACE,{"disambiguationData":[TD([[makeQuery(id+"F8.imprint","IMPRINT",EDGE,{"derivedFrom":sQuery(id+"F8.wireOp",EDGE,"E16.sketch_text.stroke-24")}),-1.0]])]});
            var Q3;
            Q3=makeQuery(id+"F8.imprint","IMPRINT",FACE,{"disambiguationData":[TD([[makeQuery(id+"F8.imprint","IMPRINT",EDGE,{"derivedFrom":sQuery(id+"F8.wireOp",EDGE,"E16.sketch_text.stroke-48")}),-1.0]])]});
            var Q4;
            Q4=makeQuery(id+"F8.imprint","IMPRINT",FACE,{"disambiguationData":[TD([[makeQuery(id+"F8.imprint","IMPRINT",EDGE,{"derivedFrom":sQuery(id+"F8.wireOp",EDGE,"E16.sketch_text.stroke-64")}),-1.0]])]});
            var Q5;
            Q5=makeQuery(id+"F8.imprint","IMPRINT",FACE,{"disambiguationData":[TD([[makeQuery(id+"F8.imprint","IMPRINT",EDGE,{"derivedFrom":sQuery(id+"F8.wireOp",EDGE,"E16.sketch_text.stroke-74")}),-1.0]])]});
            extrude(context, id + "F9", {"entities" : qUnion([Q0, Q1, Q2, Q3, Q4, Q5]), "operationType" : NewBodyOperationType.REMOVE, "oppositeDirection" : true, "depth" : 2 * mm, "offsetDistance" : 25 * mm});
        }
        {
            var Q0;
            Q0=qCreatedBy(makeId("Front.planeOp"),FACE);
            var sketch = newSketch(context, id + "F10", { "sketchPlane" : qUnion([Q0])});
            skLineSegment(sketch, "E22.bottom", {"start": v(100, 50) * mm, "end": v(-100, 50) * mm});
            skLineSegment(sketch, "E22.top", {"start": v(100, -50) * mm, "end": v(-100, -50) * mm});
            skLineSegment(sketch, "E22.left", {"start": v(100, 50) * mm, "end": v(100, -50) * mm});
            skLineSegment(sketch, "E22.right", {"start": v(-100, 50) * mm, "end": v(-100, -50) * mm});
            skSolve(sketch);
        }
        {
            var Q0;
            Q0 = qSketchRegion(id + "F10", true);
            extrude(context, id + "F11", {"entities" : qUnion([Q0]), "oppositeDirection" : true, "depth" : 1 * mm, "offsetDistance" : 25 * mm});
        }
        {
            var Q0;
            Q0=makeQuery(id+"F11.opExtrude","SWEPT_EDGE",EDGE,{"disambiguationData":[OSD([sQuery(id+"F10.wireOp",EDGE,"E22.bottom"),sQuery(id+"F10.wireOp",EDGE,"E22.left")])]});
            var Q1;
            Q1=makeQuery(id+"F11.opExtrude","SWEPT_EDGE",EDGE,{"disambiguationData":[OSD([sQuery(id+"F10.wireOp",EDGE,"E22.bottom"),sQuery(id+"F10.wireOp",EDGE,"E22.right")])]});
            fillet(context, id + "F12", {"entities" : qUnion([Q0, Q1]), "radius" : 5 * mm, "tangentPropagation" : true, "allowEdgeOverflow" : false});
        }
        {
            var Q0;
            Q0=makeQuery(id+"F11.opExtrude","CAP_EDGE",EDGE,{"disambiguationData":[OSD([sQuery(id+"F10.wireOp",EDGE,"E22.right")])],"isStart":false});
            fillet(context, id + "F13", {"entities" : qUnion([Q0]), "radius" : 3 * mm, "tangentPropagation" : true, "allowEdgeOverflow" : false});
        }
        {
            var Q0;
            Q0=makeQuery(id+"F11.opExtrude","CAP_FACE",FACE,{"disambiguationData":[OSD([sQuery(id+"F10.wireOp",EDGE,"E22.bottom"),sQuery(id+"F10.wireOp",EDGE,"E22.top"),sQuery(id+"F10.wireOp",EDGE,"E22.left"),sQuery(id+"F10.wireOp",EDGE,"E22.right")])],"isStart":false});
            var Q1;
            Q1=makeQuery(id+"F6.opFillet","BLEND_FACE",FACE,{"disambiguationData":[OSD([sQuery(id+"F0.wireOp",EDGE,"E0.top")])]});
            var Q2;
            Q2=makeQuery(id+"F3.opExtrude","SWEPT_BODY",BODY,{"disambiguationData":[OSD([sQuery(id+"F0.wireOp",EDGE,"E0.bottom"),sQuery(id+"F0.wireOp",EDGE,"E0.top"),sQuery(id+"F0.wireOp",EDGE,"E0.left"),sQuery(id+"F0.wireOp",EDGE,"E0.right"),sQuery(id+"F0.wireOp",EDGE,"E3.sketch_text.stroke-0"),sQuery(id+"F0.wireOp",EDGE,"E3.sketch_text.stroke-1"),sQuery(id+"F0.wireOp",EDGE,"E3.sketch_text.stroke-2"),sQuery(id+"F0.wireOp",EDGE,"E3.sketch_text.stroke-3"),sQuery(id+"F0.wireOp",EDGE,"E3.sketch_text.stroke-4"),sQuery(id+"F0.wireOp",EDGE,"E3.sketch_text.stroke-5"),sQuery(id+"F0.wireOp",EDGE,"E3.sketch_text.stroke-6"),sQuery(id+"F0.wireOp",EDGE,"E3.sketch_text.stroke-7"),sQuery(id+"F0.wireOp",EDGE,"E3.sketch_text.stroke-8"),sQuery(id+"F0.wireOp",EDGE,"E3.sketch_text.stroke-9"),sQuery(id+"F0.wireOp",EDGE,"E3.sketch_text.stroke-10"),sQuery(id+"F0.wireOp",EDGE,"E3.sketch_text.stroke-11"),sQuery(id+"F0.wireOp",EDGE,"E3.sketch_text.stroke-12"),sQuery(id+"F0.wireOp",EDGE,"E3.sketch_text.stroke-13"),sQuery(id+"F0.wireOp",EDGE,"E3.sketch_text.stroke-14"),sQuery(id+"F0.wireOp",EDGE,"E3.sketch_text.stroke-15"),sQuery(id+"F0.wireOp",EDGE,"E3.sketch_text.stroke-20"),sQuery(id+"F0.wireOp",EDGE,"E3.sketch_text.stroke-21"),sQuery(id+"F0.wireOp",EDGE,"E3.sketch_text.stroke-22"),sQuery(id+"F0.wireOp",EDGE,"E3.sketch_text.stroke-23"),sQuery(id+"F0.wireOp",EDGE,"E3.sketch_text.stroke-24"),sQuery(id+"F0.wireOp",EDGE,"E3.sketch_text.stroke-25"),sQuery(id+"F0.wireOp",EDGE,"E3.sketch_text.stroke-26"),sQuery(id+"F0.wireOp",EDGE,"E3.sketch_text.stroke-27"),sQuery(id+"F0.wireOp",EDGE,"E3.sketch_text.stroke-28"),sQuery(id+"F0.wireOp",EDGE,"E3.sketch_text.stroke-29"),sQuery(id+"F0.wireOp",EDGE,"E3.sketch_text.stroke-30"),sQuery(id+"F0.wireOp",EDGE,"E3.sketch_text.stroke-31"),sQuery(id+"F0.wireOp",EDGE,"E3.sketch_text.stroke-32"),sQuery(id+"F0.wireOp",EDGE,"E3.sketch_text.stroke-33"),sQuery(id+"F0.wireOp",EDGE,"E3.sketch_text.stroke-34"),sQuery(id+"F0.wireOp",EDGE,"E3.sketch_text.stroke-35"),sQuery(id+"F0.wireOp",EDGE,"E3.sketch_text.stroke-36"),sQuery(id+"F0.wireOp",EDGE,"E3.sketch_text.stroke-37"),sQuery(id+"F0.wireOp",EDGE,"E3.sketch_text.stroke-38"),sQuery(id+"F0.wireOp",EDGE,"E3.sketch_text.stroke-39"),sQuery(id+"F0.wireOp",EDGE,"E3.sketch_text.stroke-40"),sQuery(id+"F0.wireOp",EDGE,"E3.sketch_text.stroke-41"),sQuery(id+"F0.wireOp",EDGE,"E3.sketch_text.stroke-42"),sQuery(id+"F0.wireOp",EDGE,"E3.sketch_text.stroke-43"),sQuery(id+"F0.wireOp",EDGE,"E3.sketch_text.stroke-44"),sQuery(id+"F0.wireOp",EDGE,"E3.sketch_text.stroke-45"),sQuery(id+"F0.wireOp",EDGE,"E3.sketch_text.stroke-46"),sQuery(id+"F0.wireOp",EDGE,"E3.sketch_text.stroke-47"),sQuery(id+"F0.wireOp",EDGE,"E3.sketch_text.stroke-48"),sQuery(id+"F0.wireOp",EDGE,"E3.sketch_text.stroke-49"),sQuery(id+"F0.wireOp",EDGE,"E3.sketch_text.stroke-50"),sQuery(id+"F0.wireOp",EDGE,"E3.sketch_text.stroke-51"),sQuery(id+"F0.wireOp",EDGE,"E3.sketch_text.stroke-52"),sQuery(id+"F0.wireOp",EDGE,"E3.sketch_text.stroke-53"),sQuery(id+"F0.wireOp",EDGE,"E4.sketch_text.stroke-0"),sQuery(id+"F0.wireOp",EDGE,"E4.sketch_text.stroke-1"),sQuery(id+"F0.wireOp",EDGE,"E4.sketch_text.stroke-2"),sQuery(id+"F0.wireOp",EDGE,"E4.sketch_text.stroke-3"),sQuery(id+"F0.wireOp",EDGE,"E4.sketch_text.stroke-4"),sQuery(id+"F0.wireOp",EDGE,"E4.sketch_text.stroke-5"),sQuery(id+"F0.wireOp",EDGE,"E4.sketch_text.stroke-6"),sQuery(id+"F0.wireOp",EDGE,"E4.sketch_text.stroke-7"),sQuery(id+"F0.wireOp",EDGE,"E4.sketch_text.stroke-8"),sQuery(id+"F0.wireOp",EDGE,"E4.sketch_text.stroke-9"),sQuery(id+"F0.wireOp",EDGE,"E4.sketch_text.stroke-10"),sQuery(id+"F0.wireOp",EDGE,"E4.sketch_text.stroke-11"),sQuery(id+"F0.wireOp",EDGE,"E4.sketch_text.stroke-12"),sQuery(id+"F0.wireOp",EDGE,"E4.sketch_text.stroke-13"),sQuery(id+"F0.wireOp",EDGE,"E4.sketch_text.stroke-14"),sQuery(id+"F0.wireOp",EDGE,"E4.sketch_text.stroke-15"),sQuery(id+"F0.wireOp",EDGE,"E4.sketch_text.stroke-16"),sQuery(id+"F0.wireOp",EDGE,"E4.sketch_text.stroke-17"),sQuery(id+"F0.wireOp",EDGE,"E4.sketch_text.stroke-18"),sQuery(id+"F0.wireOp",EDGE,"E4.sketch_text.stroke-19"),sQuery(id+"F0.wireOp",EDGE,"E4.sketch_text.stroke-20"),sQuery(id+"F0.wireOp",EDGE,"E4.sketch_text.stroke-21"),sQuery(id+"F0.wireOp",EDGE,"E4.sketch_text.stroke-22"),sQuery(id+"F0.wireOp",EDGE,"E4.sketch_text.stroke-23"),sQuery(id+"F0.wireOp",EDGE,"E4.sketch_text.stroke-24"),sQuery(id+"F0.wireOp",EDGE,"E4.sketch_text.stroke-25"),sQuery(id+"F0.wireOp",EDGE,"E4.sketch_text.stroke-26"),sQuery(id+"F0.wireOp",EDGE,"E4.sketch_text.stroke-27"),sQuery(id+"F0.wireOp",EDGE,"E4.sketch_text.stroke-28"),sQuery(id+"F0.wireOp",EDGE,"E4.sketch_text.stroke-29"),sQuery(id+"F0.wireOp",EDGE,"E4.sketch_text.stroke-30"),sQuery(id+"F0.wireOp",EDGE,"E4.sketch_text.stroke-31"),sQuery(id+"F0.wireOp",EDGE,"E4.sketch_text.stroke-32"),sQuery(id+"F0.wireOp",EDGE,"E4.sketch_text.stroke-33"),sQuery(id+"F0.wireOp",EDGE,"E4.sketch_text.stroke-34"),sQuery(id+"F0.wireOp",EDGE,"E4.sketch_text.stroke-35"),sQuery(id+"F0.wireOp",EDGE,"E4.sketch_text.stroke-36"),sQuery(id+"F0.wireOp",EDGE,"E4.sketch_text.stroke-37"),sQuery(id+"F0.wireOp",EDGE,"E4.sketch_text.stroke-38"),sQuery(id+"F0.wireOp",EDGE,"E4.sketch_text.stroke-39"),sQuery(id+"F0.wireOp",EDGE,"E4.sketch_text.stroke-40"),sQuery(id+"F0.wireOp",EDGE,"E4.sketch_text.stroke-41"),sQuery(id+"F0.wireOp",EDGE,"E4.sketch_text.stroke-42"),sQuery(id+"F0.wireOp",EDGE,"E4.sketch_text.stroke-43"),sQuery(id+"F0.wireOp",EDGE,"E4.sketch_text.stroke-44"),sQuery(id+"F0.wireOp",EDGE,"E4.sketch_text.stroke-45"),sQuery(id+"F0.wireOp",EDGE,"E4.sketch_text.stroke-46"),sQuery(id+"F0.wireOp",EDGE,"E4.sketch_text.stroke-47"),sQuery(id+"F0.wireOp",EDGE,"E4.sketch_text.stroke-48"),sQuery(id+"F0.wireOp",EDGE,"E4.sketch_text.stroke-49"),sQuery(id+"F0.wireOp",EDGE,"E4.sketch_text.stroke-50"),sQuery(id+"F0.wireOp",EDGE,"E4.sketch_text.stroke-51"),sQuery(id+"F0.wireOp",EDGE,"E4.sketch_text.stroke-52"),sQuery(id+"F0.wireOp",EDGE,"E4.sketch_text.stroke-53"),sQuery(id+"F0.wireOp",EDGE,"E4.sketch_text.stroke-54"),sQuery(id+"F0.wireOp",EDGE,"E4.sketch_text.stroke-55"),sQuery(id+"F0.wireOp",EDGE,"E4.sketch_text.stroke-56"),sQuery(id+"F0.wireOp",EDGE,"E4.sketch_text.stroke-57"),sQuery(id+"F0.wireOp",EDGE,"E4.sketch_text.stroke-58"),sQuery(id+"F0.wireOp",EDGE,"E4.sketch_text.stroke-59"),sQuery(id+"F0.wireOp",EDGE,"E4.sketch_text.stroke-60"),sQuery(id+"F0.wireOp",EDGE,"E4.sketch_text.stroke-61"),sQuery(id+"F0.wireOp",EDGE,"E4.sketch_text.stroke-62"),sQuery(id+"F0.wireOp",EDGE,"E4.sketch_text.stroke-63"),sQuery(id+"F0.wireOp",EDGE,"E4.sketch_text.stroke-64"),sQuery(id+"F0.wireOp",EDGE,"E4.sketch_text.stroke-65"),sQuery(id+"F0.wireOp",EDGE,"E4.sketch_text.stroke-66"),sQuery(id+"F0.wireOp",EDGE,"E4.sketch_text.stroke-67"),sQuery(id+"F0.wireOp",EDGE,"E4.sketch_text.stroke-68"),sQuery(id+"F0.wireOp",EDGE,"E4.sketch_text.stroke-69"),sQuery(id+"F0.wireOp",EDGE,"E4.sketch_text.stroke-70"),sQuery(id+"F0.wireOp",EDGE,"E4.sketch_text.stroke-71"),sQuery(id+"F0.wireOp",EDGE,"E4.sketch_text.stroke-72"),sQuery(id+"F0.wireOp",EDGE,"E4.sketch_text.stroke-73"),sQuery(id+"F0.wireOp",EDGE,"E4.sketch_text.stroke-74"),sQuery(id+"F0.wireOp",EDGE,"E4.sketch_text.stroke-75"),sQuery(id+"F0.wireOp",EDGE,"E4.sketch_text.stroke-76"),sQuery(id+"F0.wireOp",EDGE,"E4.sketch_text.stroke-77"),sQuery(id+"F0.wireOp",EDGE,"E4.sketch_text.stroke-78"),sQuery(id+"F0.wireOp",EDGE,"E4.sketch_text.stroke-79"),sQuery(id+"F0.wireOp",EDGE,"E4.sketch_text.stroke-80"),sQuery(id+"F0.wireOp",EDGE,"E4.sketch_text.stroke-81"),sQuery(id+"F0.wireOp",EDGE,"E4.sketch_text.stroke-82"),sQuery(id+"F0.wireOp",EDGE,"E4.sketch_text.stroke-83"),sQuery(id+"F0.wireOp",EDGE,"E4.sketch_text.stroke-84"),sQuery(id+"F0.wireOp",EDGE,"E4.sketch_text.stroke-85"),sQuery(id+"F0.wireOp",EDGE,"E4.sketch_text.stroke-90"),sQuery(id+"F0.wireOp",EDGE,"E4.sketch_text.stroke-91"),sQuery(id+"F0.wireOp",EDGE,"E4.sketch_text.stroke-92"),sQuery(id+"F0.wireOp",EDGE,"E4.sketch_text.stroke-93"),sQuery(id+"F0.wireOp",EDGE,"E4.sketch_text.stroke-94"),sQuery(id+"F0.wireOp",EDGE,"E4.sketch_text.stroke-95"),sQuery(id+"F0.wireOp",EDGE,"E4.sketch_text.stroke-96"),sQuery(id+"F0.wireOp",EDGE,"E4.sketch_text.stroke-97"),sQuery(id+"F0.wireOp",EDGE,"E4.sketch_text.stroke-98"),sQuery(id+"F0.wireOp",EDGE,"E4.sketch_text.stroke-99"),sQuery(id+"F0.wireOp",EDGE,"E4.sketch_text.stroke-100"),sQuery(id+"F0.wireOp",EDGE,"E4.sketch_text.stroke-101"),sQuery(id+"F0.wireOp",EDGE,"E4.sketch_text.stroke-102"),sQuery(id+"F0.wireOp",EDGE,"E4.sketch_text.stroke-103"),sQuery(id+"F0.wireOp",EDGE,"E4.sketch_text.stroke-104"),sQuery(id+"F0.wireOp",EDGE,"E4.sketch_text.stroke-105"),sQuery(id+"F0.wireOp",EDGE,"E4.sketch_text.stroke-106"),sQuery(id+"F0.wireOp",EDGE,"E4.sketch_text.stroke-107"),sQuery(id+"F0.wireOp",EDGE,"E4.sketch_text.stroke-108"),sQuery(id+"F0.wireOp",EDGE,"E4.sketch_text.stroke-109"),sQuery(id+"F0.wireOp",EDGE,"E4.sketch_text.stroke-110"),sQuery(id+"F0.wireOp",EDGE,"E4.sketch_text.stroke-111"),sQuery(id+"F0.wireOp",EDGE,"E4.sketch_text.stroke-112"),sQuery(id+"F0.wireOp",EDGE,"E4.sketch_text.stroke-113"),sQuery(id+"F0.wireOp",EDGE,"E4.sketch_text.stroke-114"),sQuery(id+"F0.wireOp",EDGE,"E4.sketch_text.stroke-115"),sQuery(id+"F0.wireOp",EDGE,"E4.sketch_text.stroke-116"),sQuery(id+"F0.wireOp",EDGE,"E4.sketch_text.stroke-117"),sQuery(id+"F0.wireOp",EDGE,"E4.sketch_text.stroke-118"),sQuery(id+"F0.wireOp",EDGE,"E4.sketch_text.stroke-119"),sQuery(id+"F0.wireOp",EDGE,"E4.sketch_text.stroke-120"),sQuery(id+"F0.wireOp",EDGE,"E4.sketch_text.stroke-121"),sQuery(id+"F0.wireOp",EDGE,"E4.sketch_text.stroke-122"),sQuery(id+"F0.wireOp",EDGE,"E4.sketch_text.stroke-123")])]});
            var Q3;
            {var subQ0=sQuery(id+"F0.wireOp",EDGE,"E0.top");var subQ1=sQuery(id+"F0.wireOp",EDGE,"E0.right");Q3=makeQuery(id+"F7.opFillet","BLEND_VERTEX",VERTEX,{"blendedFrom":[makeQuery(id+"F3.opExtrude","SWEPT_EDGE",EDGE,{"disambiguationData":[OSD([subQ0,subQ1])]}),makeQuery(id+"F6.opFillet","BLEND_EDGE",EDGE,{"blendedFrom":[makeQuery(id+"F3.opExtrude","CAP_EDGE",EDGE,{"disambiguationData":[OSD([subQ0])],"isStart":false}),makeQuery(id+"F3.opExtrude","CAP_EDGE",EDGE,{"disambiguationData":[OSD([subQ1])],"isStart":false})],"blendedInto":[]}),makeQuery(id+"F6.opFillet","BLEND_FACE",FACE,{"disambiguationData":[OSD([subQ0])]}),makeQuery(id+"F3.opExtrude","SWEPT_FACE",FACE,{"disambiguationData":[OSD([subQ0])]})],"blendedInto":[makeQuery(id+"F6.opFillet","BLEND_FACE",FACE,{"disambiguationData":[OSD([subQ0])]}),makeQuery(id+"F3.opExtrude","SWEPT_FACE",FACE,{"disambiguationData":[OSD([subQ0])]})]});}
            extrude(context, id + "F14", {"entities" : qUnion([Q0]), "endBound" : BoundingType.UP_TO_VERTEX, "oppositeDirection" : true, "depth" : 10 * mm, "endBoundEntityFace" : qUnion([Q1]), "endBoundEntityBody" : qUnion([Q2]), "endBoundEntityVertex" : qUnion([Q3]), "offsetDistance" : 25 * mm});
        }
    });
